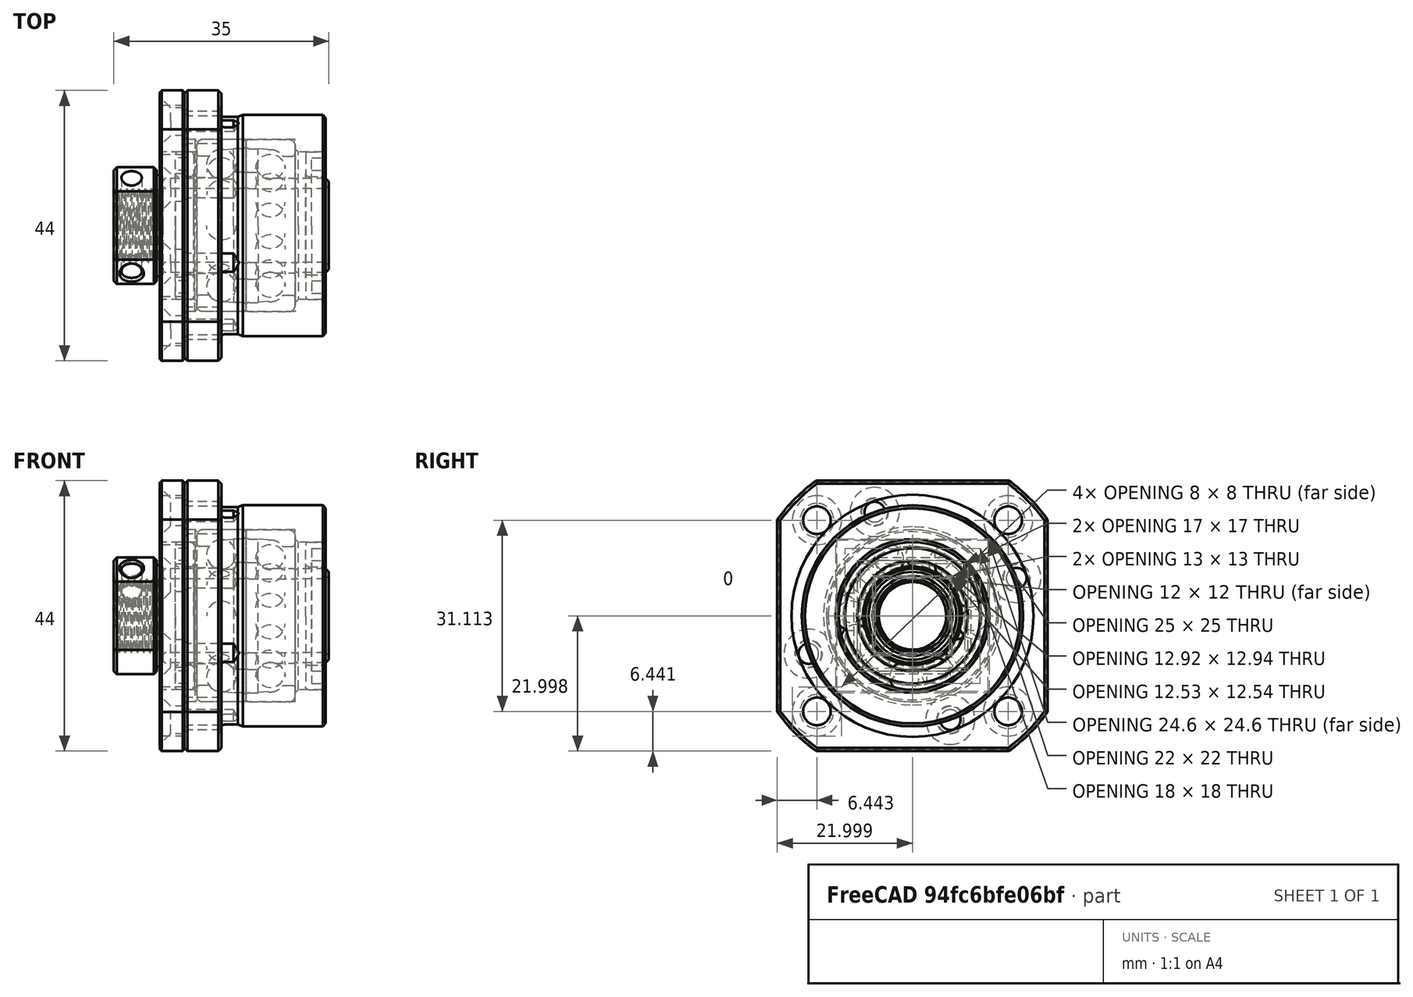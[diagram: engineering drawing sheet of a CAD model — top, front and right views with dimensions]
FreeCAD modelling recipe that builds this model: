
FCSTD DOCUMENT  (FreeCAD 0.21R38887 (Git))
Label: СтанинаСборка
License: All rights reserved
LicenseURL: http://en.wikipedia.org/wiki/All_rights_reserved
objects: Part::FeaturePython×151, App::FeaturePython×121, Part::Feature×35, App::LinkElement×20, App::Link×12, Part::Compound2×1
note: 182 computed .brp shape members not serialized (recipe doc carries the construction recipe); baked Part::Feature solids carry a one-line shape summary decoded from their .brp
EXTERNAL_REF file=ПластинаY.FCStd obj=Body
EXTERNAL_REF file=ПластинаY2.FCStd obj=Body
EXTERNAL_REF file=NEMA23.FCStd obj=Assembly
EXTERNAL_REF file=ТаблицаПараметров.FCStd obj=Spreadsheet001
EXTERNAL_REF file=ТаблицаПараметров.FCStd obj=Spreadsheet007
EXTERNAL_REF file=ЗащитаЛеваяY.FCStd obj=Body
EXTERNAL_REF file=ЗащитаПраваяY.FCStd obj=Body
EXTERNAL_REF file=РоликY.FCStd obj=Assembly
EXTERNAL_REF file=ТаблицаПараметров.FCStd obj=Spreadsheet002
EXTERNAL_REF file=ШВПY.FCStd obj=Cut001
EXTERNAL_REF file=mufta8x10.FCStd obj=Assembly
EXTERNAL_REF file=Крепеж.FCStd obj=Assembly005
EXTERNAL_REF file=Крепеж.FCStd obj=Assembly
EXTERNAL_REF file=Крепеж.FCStd obj=Assembly006

FEATURE [App::Link] Link001  label="PlateY1"
  AutoLinkLabel = true
  AutoPlacement = true
  LinkPlacement = pos=(-19.134,-17.037,0) rot=(0,0,1;0rad)
  LinkedObject = -> <external ПластинаY.FCStd>#Body
  Placement = pos=(-19.134,-17.037,0) rot=(0,0,1;0rad)
  SyncGroupVisibility = false
  TreeRank = 1
  _LinkVersion = 1
FEATURE [App::Link] Link002  label="PlateY2"
  AutoLinkLabel = true
  AutoPlacement = true
  LinkPlacement = pos=(-481.358,-61.5083,250) rot=(0,0,1;0rad)
  LinkedObject = -> <external ПластинаY2.FCStd>#Body
  Placement = pos=(-481.358,-61.5083,250) rot=(0,0,1;0rad)
  SyncGroupVisibility = false
  TreeRank = 2
  _LinkVersion = 1
FEATURE [Part::Feature] Solid
  InvalidShape = false
  TreeRank = 98
  ValidateShape = false
  shape: bbox 9.525 x 13.65 x 18.88 mm, 2 faces (baked)
FEATURE [Part::Feature] Solid001
  InvalidShape = false
  TreeRank = 99
  ValidateShape = false
  shape: bbox 8 x 34.8 x 17.4 mm, 22 faces (baked)
FEATURE [Part::Feature] Solid002
  InvalidShape = false
  TreeRank = 100
  ValidateShape = false
  shape: bbox 9.525 x 19.51 x 7.225 mm, 2 faces (baked)
FEATURE [Part::Feature] Solid003
  InvalidShape = false
  TreeRank = 101
  ValidateShape = false
  shape: bbox 9.525 x 13.65 x 18.88 mm, 2 faces (baked)
FEATURE [Part::Feature] Solid004
  InvalidShape = false
  TreeRank = 102
  ValidateShape = false
  shape: bbox 5.5 x 30.6 x 15.3 mm, 14 faces (baked)
FEATURE [Part::Feature] Solid005
  InvalidShape = false
  TreeRank = 103
  ValidateShape = false
  shape: bbox 9.525 x 15.39 x 18.01 mm, 2 faces (baked)
FEATURE [Part::Feature] Solid006
  InvalidShape = false
  TreeRank = 104
  ValidateShape = false
  shape: bbox 9.525 x 18.88 x 13.65 mm, 2 faces (baked)
FEATURE [Part::Feature] Solid007
  InvalidShape = false
  TreeRank = 105
  ValidateShape = false
  shape: bbox 9.525 x 19.43 x 11.68 mm, 2 faces (baked)
FEATURE [Part::Feature] Solid008
  InvalidShape = false
  TreeRank = 106
  ValidateShape = false
  shape: bbox 9.525 x 18.88 x 13.65 mm, 2 faces (baked)
FEATURE [Part::Feature] Solid009
  InvalidShape = false
  TreeRank = 107
  ValidateShape = false
  shape: bbox 9.525 x 11.68 x 19.43 mm, 2 faces (baked)
FEATURE [Part::Feature] Solid010
  InvalidShape = false
  TreeRank = 108
  ValidateShape = false
  shape: bbox 9.525 x 13.65 x 18.88 mm, 2 faces (baked)
FEATURE [Part::Feature] Solid011
  InvalidShape = false
  TreeRank = 109
  ValidateShape = false
  shape: bbox 9.525 x 4.763 x 19.05 mm, 2 faces (baked)
FEATURE [Part::Feature] Solid012
  InvalidShape = false
  TreeRank = 110
  ValidateShape = false
  shape: bbox 9.525 x 19.51 x 7.225 mm, 2 faces (baked)
FEATURE [Part::Feature] Solid013
  InvalidShape = false
  TreeRank = 111
  ValidateShape = false
  shape: bbox 9.525 x 15.39 x 18.01 mm, 2 faces (baked)
FEATURE [Part::Feature] Solid014
  InvalidShape = false
  TreeRank = 112
  ValidateShape = false
  shape: bbox 9.525 x 18.01 x 15.39 mm, 2 faces (baked)
FEATURE [Part::Feature] Solid015
  InvalidShape = false
  TreeRank = 113
  ValidateShape = false
  shape: bbox 3 x 24 x 48 mm, 20 faces (baked)
FEATURE [Part::Feature] Solid016
  InvalidShape = false
  TreeRank = 114
  ValidateShape = false
  shape: bbox 8 x 47.26 x 62.45 mm, 26 faces (baked)
FEATURE [Part::Feature] Solid017
  InvalidShape = false
  TreeRank = 115
  ValidateShape = false
  shape: bbox 9.525 x 18.01 x 15.39 mm, 2 faces (baked)
FEATURE [Part::Feature] Solid018
  InvalidShape = false
  TreeRank = 116
  ValidateShape = false
  shape: bbox 9.525 x 19.43 x 11.68 mm, 2 faces (baked)
FEATURE [Part::Feature] Solid019
  InvalidShape = false
  TreeRank = 117
  ValidateShape = false
  shape: bbox 9.525 x 13.65 x 18.88 mm, 2 faces (baked)
FEATURE [Part::Feature] Solid020
  InvalidShape = false
  TreeRank = 118
  ValidateShape = false
  shape: bbox 8 x 29.37 x 38.81 mm, 22 faces (baked)
FEATURE [Part::Feature] Solid021
  InvalidShape = false
  TreeRank = 119
  ValidateShape = false
  shape: bbox 8 x 56 x 28 mm, 26 faces (baked)
FEATURE [Part::Feature] Solid022
  InvalidShape = false
  TreeRank = 120
  ValidateShape = false
  shape: bbox 9.525 x 4.763 x 19.05 mm, 2 faces (baked)
FEATURE [Part::Feature] Solid023
  InvalidShape = false
  TreeRank = 121
  ValidateShape = false
  shape: bbox 9.525 x 19.05 x 4.763 mm, 2 faces (baked)
FEATURE [Part::Feature] Solid024
  InvalidShape = false
  TreeRank = 122
  ValidateShape = false
  shape: bbox 3 x 24 x 48 mm, 20 faces (baked)
FEATURE [Part::Feature] Solid025
  InvalidShape = false
  TreeRank = 123
  ValidateShape = false
  shape: bbox 9.525 x 18.88 x 13.65 mm, 2 faces (baked)
FEATURE [Part::Feature] Solid026
  InvalidShape = false
  TreeRank = 124
  ValidateShape = false
  shape: bbox 9.525 x 7.225 x 19.51 mm, 2 faces (baked)
FEATURE [Part::Feature] Solid027
  InvalidShape = false
  TreeRank = 125
  ValidateShape = false
  shape: bbox 9.167 x 19 x 19 mm, 80 faces (baked)
FEATURE [Part::Feature] Solid028
  InvalidShape = false
  TreeRank = 126
  ValidateShape = false
  shape: bbox 9.525 x 11.68 x 19.43 mm, 2 faces (baked)
FEATURE [Part::Feature] Solid029
  InvalidShape = false
  TreeRank = 127
  ValidateShape = false
  shape: bbox 5.5 x 30.6 x 15.3 mm, 14 faces (baked)
FEATURE [Part::Feature] Solid030
  InvalidShape = false
  TreeRank = 128
  ValidateShape = false
  shape: bbox 23 x 44 x 44 mm, 94 faces (baked)
FEATURE [Part::Feature] Solid031
  InvalidShape = false
  TreeRank = 129
  ValidateShape = false
  shape: bbox 9.525 x 18.88 x 13.65 mm, 2 faces (baked)
FEATURE [Part::Feature] Solid032
  InvalidShape = false
  TreeRank = 130
  ValidateShape = false
  shape: bbox 6 x 44 x 44 mm, 61 faces (baked)
FEATURE [Part::Feature] Solid033
  InvalidShape = false
  TreeRank = 131
  ValidateShape = false
  shape: bbox 9.525 x 19.05 x 4.763 mm, 2 faces (baked)
FEATURE [Part::Feature] Solid034
  InvalidShape = false
  TreeRank = 132
  ValidateShape = false
  shape: bbox 9.525 x 7.225 x 19.51 mm, 2 faces (baked)
FEATURE [Part::Compound2] Compound  label="FK12"
  InvalidShape = false
  Links = -> [Solid,Solid001,Solid002,Solid003,Solid004,Solid005,Solid006,Solid007,Solid008,Solid009,Solid010,Solid011,Solid012,Solid013,Solid014,Solid015,Solid016,Solid017,Solid018,Solid019,Solid020,Solid021,Solid022,Solid023,Solid024,Solid025,Solid026,Solid027,Solid028,Solid029,Solid030,Solid031,Solid032,Solid033,Solid034]
  Placement = pos=(282.718,411.762,278.225) rot=(-0.707107,0,-0.707107;3.14159rad)
  TreeRank = 133
  ValidateShape = false
FEATURE [App::Link] Link003  label="NEMA23"
  AutoLinkLabel = true
  AutoPlacement = true
  LinkPlacement = pos=(205.55,418.707,297.9) rot=(0,1,0;3.14159rad)
  LinkedObject = -> <external NEMA23.FCStd>#Assembly
  Placement = pos=(205.55,418.707,297.9) rot=(0,1,0;3.14159rad)
  SyncGroupVisibility = false
  TreeRank = 164
  _LinkVersion = 1
FEATURE [App::Link] Link012  label="ЗащитаСлеваY"
  AutoLinkLabel = false
  AutoPlacement = true
  LinkedObject = -> <external ЗащитаЛеваяY.FCStd>#Body
  SyncGroupVisibility = false
  TreeRank = 458
  _LinkOwner = 1626
  _LinkVersion = 1
FEATURE [App::Link] Link013  label="ЗащитаСправаY"
  AutoLinkLabel = false
  AutoPlacement = true
  LinkPlacement = pos=(1.421e-13,-1.35e-13,223.3) rot=(0,0,1;0rad)
  LinkedObject = -> <external ЗащитаПраваяY.FCStd>#Body
  Placement = pos=(1.421e-13,-1.35e-13,223.3) rot=(0,0,1;0rad)
  SyncGroupVisibility = false
  TreeRank = 459
  _LinkOwner = 1626
  _LinkVersion = 1
FEATURE [App::Link] Link018  label="ШВПY"
  AutoLinkLabel = true
  AutoPlacement = true
  LinkPlacement = pos=(377.35,390.502,185) rot=(1,0,0;1.5708rad)
  LinkedObject = -> <external ШВПY.FCStd>#Cut001
  Placement = pos=(377.35,390.502,185) rot=(1,0,0;1.5708rad)
  SyncGroupVisibility = false
  TreeRank = 610
  _LinkVersion = 1
FEATURE [App::Link] Link019  label="Муфта_8_10мм001"
  AutoLinkLabel = true
  AutoPlacement = true
  LinkPlacement = pos=(390.615,406.393,319.227) rot=(0.199343,-0.787324,-0.583424;3.79561rad)
  LinkedObject = -> <external mufta8x10.FCStd>#Assembly
  Placement = pos=(390.615,406.393,319.227) rot=(0.199343,-0.787324,-0.583424;3.79561rad)
  SyncGroupVisibility = false
  TreeRank = 617
  _LinkVersion = 1
FEATURE [App::LinkElement] Link014_i0
  LinkPlacement = pos=(33.3,-2.65,-2.65) rot=(1,0,0;3.14159rad)
  LinkedObject = -> <external РоликY.FCStd>#Assembly
  Placement = pos=(33.3,-2.65,-2.65) rot=(1,0,0;3.14159rad)
  TreeRank = 818
  _LinkOwner = 1707
  _LinkVersion = 1
FEATURE [App::LinkElement] Link014_i1
  LinkPlacement = pos=(35.1,110.35,-2.65) rot=(0,-1,0;3.14159rad)
  LinkedObject = -> <external РоликY.FCStd>#Assembly
  Placement = pos=(35.1,110.35,-2.65) rot=(0,-1,0;3.14159rad)
  TreeRank = 819
  _LinkOwner = 1707
  _LinkVersion = 1
FEATURE [App::LinkElement] Link014_i2
  LinkPlacement = pos=(33.3,-2.65,511.35) rot=(1,0,0;3.14159rad)
  LinkedObject = -> <external РоликY.FCStd>#Assembly
  Placement = pos=(33.3,-2.65,511.35) rot=(1,0,0;3.14159rad)
  TreeRank = 820
  _LinkOwner = 1707
  _LinkVersion = 1
FEATURE [App::LinkElement] Link014_i3
  LinkPlacement = pos=(33.3,110.35,511.35) rot=(1,0,0;3.14159rad)
  LinkedObject = -> <external РоликY.FCStd>#Assembly
  Placement = pos=(33.3,110.35,511.35) rot=(1,0,0;3.14159rad)
  TreeRank = 821
  _LinkOwner = 1707
  _LinkVersion = 1
FEATURE [App::Link] Link014  label="Ролики"
  AutoLinkLabel = true
  AutoPlacement = true
  ElementCount = 4
  ElementList = -> [Link014_i0,Link014_i1,Link014_i2,Link014_i3]
  LinkPlacement = pos=(-234.35,38.35,78.7) rot=(-0.707107,0,-0.707107;3.14159rad)
  LinkedObject = -> <external РоликY.FCStd>#Assembly
  Placement = pos=(-234.35,38.35,78.7) rot=(-0.707107,0,-0.707107;3.14159rad)
  SyncGroupVisibility = false
  TreeRank = 485
  _LinkVersion = 1
FEATURE [Part::FeaturePython] Parts004  # WARN: FeaturePython — macro-defined, semantics opaque (R4)
  Group = -> [Link012,Link013,Link014]
  GroupMode = 0
  InvalidShape = false
  TreeRank = 457
  ValidateShape = false
  _LinkVersion = 1
FEATURE [App::LinkElement] Link030_i0
  LinkPlacement = pos=(417.35,350.007,2.01454e-09) rot=(0,0,1;0rad)
  LinkedObject = -> <external Крепеж.FCStd>#Assembly005
  Placement = pos=(417.35,350.007,2.01454e-09) rot=(0,0,1;0rad)
  TreeRank = 867
  _LinkOwner = 2156
  _LinkVersion = 1
FEATURE [App::LinkElement] Link030_i1
  LinkPlacement = pos=(417.35,310.007,2.01454e-09) rot=(0,0,1;0rad)
  LinkedObject = -> <external Крепеж.FCStd>#Assembly005
  Placement = pos=(417.35,310.007,2.01454e-09) rot=(0,0,1;0rad)
  TreeRank = 868
  _LinkOwner = 2156
  _LinkVersion = 1
FEATURE [App::LinkElement] Link030_i2
  LinkPlacement = pos=(337.35,310.007,2.01459e-09) rot=(0,0,1;0rad)
  LinkedObject = -> <external Крепеж.FCStd>#Assembly005
  Placement = pos=(337.35,310.007,2.01459e-09) rot=(0,0,1;0rad)
  TreeRank = 869
  _LinkOwner = 2156
  _LinkVersion = 1
FEATURE [App::LinkElement] Link030_i3
  LinkPlacement = pos=(337.35,350.007,2.01458e-09) rot=(0,0,1;0rad)
  LinkedObject = -> <external Крепеж.FCStd>#Assembly005
  Placement = pos=(337.35,350.007,2.01458e-09) rot=(0,0,1;0rad)
  TreeRank = 870
  _LinkOwner = 2156
  _LinkVersion = 1
FEATURE [App::LinkElement] Link030_i4
  LinkPlacement = pos=(337.35,310.007,420) rot=(1,0,0;3.14159rad)
  LinkedObject = -> <external Крепеж.FCStd>#Assembly005
  Placement = pos=(337.35,310.007,420) rot=(1,0,0;3.14159rad)
  TreeRank = 871
  _LinkOwner = 2156
  _LinkVersion = 1
FEATURE [App::LinkElement] Link030_i5
  LinkPlacement = pos=(417.35,310.007,420) rot=(1,0,0;3.14159rad)
  LinkedObject = -> <external Крепеж.FCStd>#Assembly005
  Placement = pos=(417.35,310.007,420) rot=(1,0,0;3.14159rad)
  TreeRank = 872
  _LinkOwner = 2156
  _LinkVersion = 1
FEATURE [App::LinkElement] Link030_i6
  LinkPlacement = pos=(417.35,350.007,420) rot=(1,0,0;3.14159rad)
  LinkedObject = -> <external Крепеж.FCStd>#Assembly005
  Placement = pos=(417.35,350.007,420) rot=(1,0,0;3.14159rad)
  TreeRank = 873
  _LinkOwner = 2156
  _LinkVersion = 1
FEATURE [App::LinkElement] Link030_i7
  LinkPlacement = pos=(337.35,350.007,420) rot=(1,0,0;3.14159rad)
  LinkedObject = -> <external Крепеж.FCStd>#Assembly005
  Placement = pos=(337.35,350.007,420) rot=(1,0,0;3.14159rad)
  TreeRank = 874
  _LinkOwner = 2156
  _LinkVersion = 1
FEATURE [App::Link] Link030  label="КрепежМ6_Тгайка"
  AutoLinkLabel = true
  AutoPlacement = true
  ElementCount = 8
  ElementList = -> [Link030_i0,Link030_i1,Link030_i2,Link030_i3,Link030_i4,Link030_i5,Link030_i6,Link030_i7]
  LinkedObject = -> <external Крепеж.FCStd>#Assembly005
  SyncGroupVisibility = false
  TreeRank = 857
  _LinkVersion = 1
FEATURE [App::LinkElement] Link031_i0
  LinkPlacement = pos=(153.78,414.077,264.8) rot=(0,0,1;3.14159rad)
  LinkedObject = -> <external Крепеж.FCStd>#Assembly
  Placement = pos=(153.78,414.077,264.8) rot=(0,0,1;3.14159rad)
  TreeRank = 909
  _LinkOwner = 2210
  _LinkVersion = 1
FEATURE [App::LinkElement] Link031_i1
  LinkPlacement = pos=(153.78,366.937,264.8) rot=(0,0,1;3.14159rad)
  LinkedObject = -> <external Крепеж.FCStd>#Assembly
  Placement = pos=(153.78,366.937,264.8) rot=(0,0,1;3.14159rad)
  TreeRank = 910
  _LinkOwner = 2210
  _LinkVersion = 1
FEATURE [App::LinkElement] Link031_i2
  LinkPlacement = pos=(200.92,366.937,264.8) rot=(0,0,1;3.14159rad)
  LinkedObject = -> <external Крепеж.FCStd>#Assembly
  Placement = pos=(200.92,366.937,264.8) rot=(0,0,1;3.14159rad)
  TreeRank = 911
  _LinkOwner = 2210
  _LinkVersion = 1
FEATURE [App::LinkElement] Link031_i3
  LinkPlacement = pos=(200.92,414.077,264.8) rot=(0,0,1;3.14159rad)
  LinkedObject = -> <external Крепеж.FCStd>#Assembly
  Placement = pos=(200.92,414.077,264.8) rot=(0,0,1;3.14159rad)
  TreeRank = 912
  _LinkOwner = 2210
  _LinkVersion = 1
FEATURE [App::Link] Link031  label="М5х12"
  AutoLinkLabel = false
  AutoPlacement = true
  ElementCount = 4
  ElementList = -> [Link031_i0,Link031_i1,Link031_i2,Link031_i3]
  LinkedObject = -> <external Крепеж.FCStd>#Assembly
  SyncGroupVisibility = false
  TreeRank = 908
  _LinkVersion = 1
FEATURE [Part::FeaturePython] Parts002  # WARN: FeaturePython — macro-defined, semantics opaque (R4)
  Group = -> [Link003,Link002,Link031]
  GroupMode = 0
  InvalidShape = false
  TreeRank = 221
  ValidateShape = false
  _LinkVersion = 1
FEATURE [App::LinkElement] Link032_i0
  LinkPlacement = pos=(194.43,377.469,-6) rot=(-1,0,0;3.14159rad)
  LinkedObject = -> <external Крепеж.FCStd>#Assembly006
  Placement = pos=(194.43,377.469,-6) rot=(-1,0,0;3.14159rad)
  TreeRank = 918
  _LinkOwner = 2219
  _LinkVersion = 1
FEATURE [App::LinkElement] Link032_i1
  LinkPlacement = pos=(194.43,346.356,-6) rot=(-1,0,0;3.14159rad)
  LinkedObject = -> <external Крепеж.FCStd>#Assembly006
  Placement = pos=(194.43,346.356,-6) rot=(-1,0,0;3.14159rad)
  TreeRank = 919
  _LinkOwner = 2219
  _LinkVersion = 1
FEATURE [App::LinkElement] Link032_i2
  LinkPlacement = pos=(225.543,346.356,-6) rot=(-1,0,0;3.14159rad)
  LinkedObject = -> <external Крепеж.FCStd>#Assembly006
  Placement = pos=(225.543,346.356,-6) rot=(-1,0,0;3.14159rad)
  TreeRank = 920
  _LinkOwner = 2219
  _LinkVersion = 1
FEATURE [App::LinkElement] Link032_i3
  LinkPlacement = pos=(225.543,377.469,-6) rot=(-1,0,0;3.14159rad)
  LinkedObject = -> <external Крепеж.FCStd>#Assembly006
  Placement = pos=(225.543,377.469,-6) rot=(-1,0,0;3.14159rad)
  TreeRank = 921
  _LinkOwner = 2219
  _LinkVersion = 1
FEATURE [App::Link] Link032  label="М4х16"
  AutoLinkLabel = true
  AutoPlacement = true
  ElementCount = 4
  ElementList = -> [Link032_i0,Link032_i1,Link032_i2,Link032_i3]
  LinkedObject = -> <external Крепеж.FCStd>#Assembly006
  SyncGroupVisibility = false
  TreeRank = 917
  _LinkVersion = 1
FEATURE [Part::FeaturePython] Parts001  # WARN: FeaturePython — macro-defined, semantics opaque (R4)
  Group = -> [Link001,Compound,Link032]
  GroupMode = 0
  InvalidShape = false
  TreeRank = 217
  ValidateShape = false
  _LinkVersion = 1
FEATURE [App::Link] Link  label="МасивПрофиля"
  AutoLinkLabel = false
  AutoPlacement = true
  LinkPlacement = pos=(0,0,0) rot=(0,1,0;1.5708rad)
  Placement = pos=(0,0,0) rot=(0,1,0;1.5708rad)
  SyncGroupVisibility = false
  TreeRank = 933
  _LinkOwner = 1573
  _LinkVersion = 1
FEATURE [Part::FeaturePython] Assembly001  label="PlateForFK12"  # WARN: FeaturePython — macro-defined, semantics opaque (R4)
  AutoRelax = true
  BuildShape = 0
  Freeze = false
  Group = -> [Constraints001,Elements001,Parts001]
  InvalidShape = false
  Placement = pos=(167.364,28.5944,2.01459e-09) rot=(0,0,1;0rad)
  TreeRank = 214
  ValidateShape = false
  Verbose = false
  _LinkVersion = 1
  _SolverType = 1
  _Version = 1
FEATURE [App::FeaturePython] Constraints001  # WARN: FeaturePython — macro-defined, semantics opaque (R4)
  Group = -> [Constraint004,Constraint001,Constraint018,Constraint021,Constraint020,Constraint019]
  TreeRank = 215
  _LinkVersion = 1
  _Version = 1
FEATURE [App::FeaturePython] Elements001  # WARN: FeaturePython — macro-defined, semantics opaque (R4)
  Group = -> [Element,Element001,Element002,Element003,Element004,Element005,Element006,Element007,Element008,Element009,Element010,_Element,Element032,Element033,Element035,Element036,_Element002,_Element003,_Element004,_Element005,_Element006,_Element007,Element038,Element040,Element041,Element042,Element046,Element082,Element098,Element100,Element102,Element104,_Element060,_Element061,_Element062,+1 more]
  TreeRank = 216
  _LinkVersion = 1
FEATURE [Part::FeaturePython] Assembly002  label="PlateForMotor"  # WARN: FeaturePython — macro-defined, semantics opaque (R4)
  AutoRelax = true
  BuildShape = 0
  Freeze = false
  Group = -> [Constraints002,Elements002,Parts002]
  InvalidShape = false
  Placement = pos=(200,5.45395e-11,160) rot=(0,0,1;0rad)
  TreeRank = 218
  ValidateShape = false
  Verbose = false
  _LinkVersion = 1
  _SolverType = 1
  _Version = 1
FEATURE [App::FeaturePython] Constraints002  # WARN: FeaturePython — macro-defined, semantics opaque (R4)
  Group = -> [Constraint007,Constraint006,Constraint060,Constraint061,Constraint062,Constraint063]
  TreeRank = 219
  _LinkVersion = 1
  _Version = 1
FEATURE [App::FeaturePython] Elements002  # WARN: FeaturePython — macro-defined, semantics opaque (R4)
  Group = -> [Element011,Element012,Element013,Element014,Element015,Element016,Element017,Element018,_Element001,Element021,Element020,Element022,Element023,_Element008,_Element009,Element037,Element039,Element048,Element051,Element073,Element087,Element106,Element108,Element110,Element112,_Element056,_Element057,_Element058,_Element059]
  TreeRank = 220
  _LinkVersion = 1
FEATURE [Part::FeaturePython] Element  # link proxy (typed FeaturePython)
  Detach = false
  InvalidShape = false
  LinkTransform = true
  LinkedObject = -> Compound [Face353]
  TreeRank = 222
  ValidateShape = false
  _LinkVersion = 1
  _Parent = -> Elements001
FEATURE [Part::FeaturePython] Element001  # link proxy (typed FeaturePython)
  Detach = false
  InvalidShape = false
  LinkTransform = true
  LinkedObject = -> Link001 [Pad.Face18]
  TreeRank = 223
  ValidateShape = false
  _LinkVersion = 1
  _Parent = -> Elements001
FEATURE [Part::FeaturePython] Element002  # link proxy (typed FeaturePython)
  Detach = false
  InvalidShape = false
  LinkTransform = true
  LinkedObject = -> Compound [Face313]
  TreeRank = 224
  ValidateShape = false
  _LinkVersion = 1
  _Parent = -> Elements001
FEATURE [Part::FeaturePython] Element003  # link proxy (typed FeaturePython)
  Detach = false
  InvalidShape = false
  LinkTransform = true
  LinkedObject = -> Compound [Face378]
  TreeRank = 225
  ValidateShape = false
  _LinkVersion = 1
  _Parent = -> Elements001
FEATURE [Part::FeaturePython] Element004  # link proxy (typed FeaturePython)
  Detach = false
  InvalidShape = false
  LinkTransform = true
  LinkedObject = -> Compound [Face301]
  TreeRank = 226
  ValidateShape = false
  _LinkVersion = 1
  _Parent = -> Elements001
FEATURE [Part::FeaturePython] Element005  # link proxy (typed FeaturePython)
  Detach = false
  InvalidShape = false
  LinkTransform = true
  LinkedObject = -> Compound [Face337]
  TreeRank = 227
  ValidateShape = false
  _LinkVersion = 1
  _Parent = -> Elements001
FEATURE [Part::FeaturePython] Element006  # link proxy (typed FeaturePython)
  Detach = false
  InvalidShape = false
  LinkTransform = true
  LinkedObject = -> Compound [Face299]
  TreeRank = 228
  ValidateShape = false
  _LinkVersion = 1
  _Parent = -> Elements001
FEATURE [Part::FeaturePython] Element007  # link proxy (typed FeaturePython)
  Detach = false
  InvalidShape = false
  LinkTransform = true
  LinkedObject = -> Compound [Face335]
  TreeRank = 229
  ValidateShape = false
  _LinkVersion = 1
  _Parent = -> Elements001
FEATURE [Part::FeaturePython] Element008  # link proxy (typed FeaturePython)
  Detach = false
  InvalidShape = false
  LinkTransform = true
  LinkedObject = -> Link001 [Pad.Face14]
  TreeRank = 230
  ValidateShape = false
  _LinkVersion = 1
  _Parent = -> Elements001
FEATURE [Part::FeaturePython] Element009  # link proxy (typed FeaturePython)
  Detach = false
  InvalidShape = false
  LinkTransform = true
  LinkedObject = -> Link001 [Pad.Face16]
  TreeRank = 231
  ValidateShape = false
  _LinkVersion = 1
  _Parent = -> Elements001
FEATURE [Part::FeaturePython] Element010  # link proxy (typed FeaturePython)
  Detach = false
  InvalidShape = false
  LinkTransform = true
  LinkedObject = -> Link001 [Pad.Face9]
  TreeRank = 232
  ValidateShape = false
  _LinkVersion = 1
  _Parent = -> Elements001
FEATURE [App::FeaturePython] Constraint001  label="Attachment"  # WARN: FeaturePython — macro-defined, semantics opaque (R4)
  Cascade = false
  Disabled = false
  Group = -> [ElementLink002,ElementLink004]
  Multiply = false
  TreeRank = 236
  _ConstraintType = 45
  _LinkVersion = 1
  _Parent = -> Constraints001
FEATURE [App::FeaturePython] ElementLink002  label="_Element002"  # link proxy (typed FeaturePython)
  LinkTransform = true
  LinkedObject = -> _Element002
  TreeRank = 237
  _LinkVersion = 1
  _Parent = -> Constraint001
FEATURE [App::FeaturePython] ElementLink004  label="_Element010"  # link proxy (typed FeaturePython)
  LinkTransform = true
  LinkedObject = -> _Element003
  TreeRank = 239
  _LinkVersion = 1
  _Parent = -> Constraint001
FEATURE [Part::FeaturePython] _Element  # link proxy (typed FeaturePython)
  Detach = false
  InvalidShape = false
  LinkTransform = true
  LinkedObject = -> Link001 [Pad.Edge9]
  TreeRank = 256
  ValidateShape = false
  _LinkVersion = 1
  _Parent = -> Elements001
FEATURE [App::FeaturePython] Constraint004  label="Locked"  # WARN: FeaturePython — macro-defined, semantics opaque (R4)
  Disabled = false
  Group = -> [ElementLink012]
  TreeRank = 260
  _ConstraintType = 0
  _LinkVersion = 1
  _Parent = -> Constraints001
FEATURE [App::FeaturePython] ElementLink012  label="Element001"  # link proxy (typed FeaturePython)
  LinkTransform = true
  LinkedObject = -> Element001
  TreeRank = 261
  _LinkVersion = 1
  _Parent = -> Constraint004
FEATURE [Part::FeaturePython] Element011  # link proxy (typed FeaturePython)
  Detach = false
  InvalidShape = false
  LinkTransform = true
  LinkedObject = -> Link002 [Chamfer001.Face5]
  TreeRank = 270
  ValidateShape = false
  _LinkVersion = 1
  _Parent = -> Elements002
FEATURE [Part::FeaturePython] Element012  # link proxy (typed FeaturePython)
  Detach = false
  InvalidShape = false
  LinkTransform = true
  LinkedObject = -> Link003 [1.$Element001.]
  TreeRank = 271
  ValidateShape = false
  _LinkVersion = 1
  _Parent = -> Elements002
FEATURE [Part::FeaturePython] Element013  # link proxy (typed FeaturePython)
  Detach = false
  InvalidShape = false
  LinkTransform = true
  LinkedObject = -> Link002 [Chamfer001.Face1]
  TreeRank = 272
  ValidateShape = false
  _LinkVersion = 1
  _Parent = -> Elements002
FEATURE [Part::FeaturePython] Element014  # link proxy (typed FeaturePython)
  Detach = false
  InvalidShape = false
  LinkTransform = true
  LinkedObject = -> Link003 [1.$Element003.]
  TreeRank = 273
  ValidateShape = false
  _LinkVersion = 1
  _Parent = -> Elements002
FEATURE [Part::FeaturePython] Element015  # link proxy (typed FeaturePython)
  Detach = false
  InvalidShape = false
  LinkTransform = true
  LinkedObject = -> Link002 [Chamfer001.Face22]
  TreeRank = 274
  ValidateShape = false
  _LinkVersion = 1
  _Parent = -> Elements002
FEATURE [Part::FeaturePython] Element016  # link proxy (typed FeaturePython)
  Detach = false
  InvalidShape = false
  LinkTransform = true
  LinkedObject = -> Link003 [1.$Element006.]
  TreeRank = 275
  ValidateShape = false
  _LinkVersion = 1
  _Parent = -> Elements002
FEATURE [Part::FeaturePython] Element017  # link proxy (typed FeaturePython)
  Detach = false
  InvalidShape = false
  LinkTransform = true
  LinkedObject = -> Link002 [Chamfer001.Face21]
  TreeRank = 276
  ValidateShape = false
  _LinkVersion = 1
  _Parent = -> Elements002
FEATURE [Part::FeaturePython] Element018  # link proxy (typed FeaturePython)
  Detach = false
  InvalidShape = false
  LinkTransform = true
  LinkedObject = -> Link003 [1.$Element007.]
  TreeRank = 277
  ValidateShape = false
  _LinkVersion = 1
  _Parent = -> Elements002
FEATURE [App::FeaturePython] Constraint006  label="Attachment005"  # WARN: FeaturePython — macro-defined, semantics opaque (R4)
  Cascade = false
  Disabled = false
  Group = -> [ElementLink016,ElementLink018]
  Multiply = false
  TreeRank = 281
  _ConstraintType = 45
  _LinkVersion = 1
  _Parent = -> Constraints002
FEATURE [App::FeaturePython] ElementLink016  label="_Element013"  # link proxy (typed FeaturePython)
  LinkTransform = true
  LinkedObject = -> _Element008
  TreeRank = 282
  _LinkVersion = 1
  _Parent = -> Constraint006
FEATURE [App::FeaturePython] Constraint007  label="Locked001"  # WARN: FeaturePython — macro-defined, semantics opaque (R4)
  Disabled = false
  Group = -> [ElementLink017]
  TreeRank = 283
  _ConstraintType = 0
  _LinkVersion = 1
  _Parent = -> Constraints002
FEATURE [App::FeaturePython] ElementLink017  label="_Element001"  # link proxy (typed FeaturePython)
  LinkTransform = true
  LinkedObject = -> _Element001
  TreeRank = 284
  _LinkVersion = 1
  _Parent = -> Constraint007
FEATURE [Part::FeaturePython] _Element001  # link proxy (typed FeaturePython)
  Detach = false
  InvalidShape = false
  LinkTransform = true
  LinkedObject = -> Link002 [Chamfer001.Face4]
  TreeRank = 285
  ValidateShape = false
  _LinkVersion = 1
  _Parent = -> Elements002
FEATURE [App::FeaturePython] ElementLink018  label="_Element014"  # link proxy (typed FeaturePython)
  LinkTransform = true
  LinkedObject = -> _Element009
  TreeRank = 286
  _LinkVersion = 1
  _Parent = -> Constraint006
FEATURE [Part::FeaturePython] Element020  label="2_plate"  # link proxy (typed FeaturePython)
  Detach = false
  InvalidShape = false
  LinkTransform = true
  LinkedObject = -> Link003 [1.$Element008.]
  TreeRank = 294
  ValidateShape = false
  _LinkVersion = 1
  _Parent = -> Elements002
FEATURE [Part::FeaturePython] Element021  label="1_plate"  # link proxy (typed FeaturePython)
  Detach = false
  InvalidShape = false
  LinkTransform = true
  LinkedObject = -> Link003 [1.$Element009.]
  TreeRank = 313
  ValidateShape = false
  _LinkVersion = 1
  _Parent = -> Elements002
FEATURE [Part::FeaturePython] Element022  label="3_plate"  # link proxy (typed FeaturePython)
  Detach = false
  InvalidShape = false
  LinkTransform = true
  LinkedObject = -> Link003 [1.$Element010.]
  TreeRank = 314
  ValidateShape = false
  _LinkVersion = 1
  _Parent = -> Elements002
FEATURE [Part::FeaturePython] Element023  label="4_plate"  # link proxy (typed FeaturePython)
  Detach = false
  InvalidShape = false
  LinkTransform = true
  LinkedObject = -> Link003 [1.$Element011.]
  TreeRank = 315
  ValidateShape = false
  _LinkVersion = 1
  _Parent = -> Elements002
FEATURE [Part::FeaturePython] Element032  label="1hole"  # link proxy (typed FeaturePython)
  Detach = false
  InvalidShape = false
  LinkTransform = true
  LinkedObject = -> Compound [Edge724]
  TreeRank = 352
  ValidateShape = false
  _LinkVersion = 1
  _Parent = -> Elements001
FEATURE [Part::FeaturePython] Element033  label="2hole"  # link proxy (typed FeaturePython)
  Detach = false
  InvalidShape = false
  LinkTransform = true
  LinkedObject = -> Compound [Edge736]
  TreeRank = 353
  ValidateShape = false
  _LinkVersion = 1
  _Parent = -> Elements001
FEATURE [Part::FeaturePython] Element035  label="3hole"  # link proxy (typed FeaturePython)
  Detach = false
  InvalidShape = false
  LinkTransform = true
  LinkedObject = -> Compound [Edge732]
  TreeRank = 355
  ValidateShape = false
  _LinkVersion = 1
  _Parent = -> Elements001
FEATURE [Part::FeaturePython] Element036  label="4hole"  # link proxy (typed FeaturePython)
  Detach = false
  InvalidShape = false
  LinkTransform = true
  LinkedObject = -> Compound [Edge728]
  TreeRank = 356
  ValidateShape = false
  _LinkVersion = 1
  _Parent = -> Elements001
FEATURE [App::FeaturePython] Constraint018  label="Attachment001"  # WARN: FeaturePython — macro-defined, semantics opaque (R4)
  Cascade = false
  Disabled = false
  Group = -> [ElementLink039,ElementLink040]
  Multiply = false
  TreeRank = 357
  _ConstraintType = 45
  _LinkVersion = 1
  _Parent = -> Constraints001
FEATURE [App::FeaturePython] ElementLink039  label="М4_16_посадка@М4х16@#3"  # link proxy (typed FeaturePython)
  LinkTransform = true
  LinkedObject = -> _Element063
  TreeRank = 358
  _LinkVersion = 1
  _Parent = -> Constraint018
FEATURE [App::FeaturePython] ElementLink040  label="4hole"  # link proxy (typed FeaturePython)
  LinkTransform = true
  LinkedObject = -> Element036
  TreeRank = 359
  _LinkVersion = 1
  _Parent = -> Constraint018
FEATURE [App::FeaturePython] Constraint019  label="Attachment004"  # WARN: FeaturePython — macro-defined, semantics opaque (R4)
  Cascade = false
  Disabled = false
  Group = -> [ElementLink041,ElementLink042]
  Multiply = false
  TreeRank = 360
  _ConstraintType = 45
  _LinkVersion = 1
  _Parent = -> Constraints001
FEATURE [App::FeaturePython] ElementLink041  label="3hole"  # link proxy (typed FeaturePython)
  LinkTransform = true
  LinkedObject = -> Element035
  TreeRank = 361
  _LinkVersion = 1
  _Parent = -> Constraint019
FEATURE [App::FeaturePython] ElementLink042  label="М4_16_посадка@М4х16@#2"  # link proxy (typed FeaturePython)
  LinkTransform = true
  LinkedObject = -> _Element062
  TreeRank = 362
  _LinkVersion = 1
  _Parent = -> Constraint019
FEATURE [App::FeaturePython] Constraint020  label="Attachment003"  # WARN: FeaturePython — macro-defined, semantics opaque (R4)
  Cascade = false
  Disabled = false
  Group = -> [ElementLink043,ElementLink044]
  Multiply = false
  TreeRank = 363
  _ConstraintType = 45
  _LinkVersion = 1
  _Parent = -> Constraints001
FEATURE [App::FeaturePython] ElementLink043  label="М4_16_посадка@М4х16@#1"  # link proxy (typed FeaturePython)
  LinkTransform = true
  LinkedObject = -> _Element061
  TreeRank = 364
  _LinkVersion = 1
  _Parent = -> Constraint020
FEATURE [App::FeaturePython] ElementLink044  label="2hole"  # link proxy (typed FeaturePython)
  LinkTransform = true
  LinkedObject = -> Element033
  TreeRank = 365
  _LinkVersion = 1
  _Parent = -> Constraint020
FEATURE [App::FeaturePython] Constraint021  label="Attachment002"  # WARN: FeaturePython — macro-defined, semantics opaque (R4)
  Cascade = false
  Disabled = false
  Group = -> [ElementLink045,ElementLink046]
  Multiply = false
  TreeRank = 366
  _ConstraintType = 45
  _LinkVersion = 1
  _Parent = -> Constraints001
FEATURE [App::FeaturePython] ElementLink045  label="М4_16_посадка@М4х16@#0"  # link proxy (typed FeaturePython)
  LinkTransform = true
  LinkedObject = -> _Element060
  TreeRank = 367
  _LinkVersion = 1
  _Parent = -> Constraint021
FEATURE [App::FeaturePython] ElementLink046  label="1hole"  # link proxy (typed FeaturePython)
  LinkTransform = true
  LinkedObject = -> Element032
  TreeRank = 368
  _LinkVersion = 1
  _Parent = -> Constraint021
FEATURE [Part::FeaturePython] _Element002  # link proxy (typed FeaturePython)
  Detach = false
  InvalidShape = false
  LinkTransform = true
  LinkedObject = -> Compound [Edge904]
  TreeRank = 384
  ValidateShape = false
  _LinkVersion = 1
  _Parent = -> Elements001
FEATURE [Part::FeaturePython] _Element003  label="_Element010"  # link proxy (typed FeaturePython)
  Detach = false
  InvalidShape = false
  LinkTransform = true
  LinkedObject = -> Link001 [Pad.Edge26]
  TreeRank = 385
  ValidateShape = false
  _LinkVersion = 1
  _Parent = -> Elements001
FEATURE [Part::FeaturePython] _Element004  label="_Element009"  # link proxy (typed FeaturePython)
  Detach = false
  InvalidShape = false
  LinkTransform = true
  LinkedObject = -> Link001 [Pad.Edge47]
  TreeRank = 386
  ValidateShape = false
  _LinkVersion = 1
  _Parent = -> Elements001
FEATURE [Part::FeaturePython] _Element005  # link proxy (typed FeaturePython)
  Detach = false
  InvalidShape = false
  LinkTransform = true
  LinkedObject = -> Compound [Edge770]
  TreeRank = 387
  ValidateShape = false
  _LinkVersion = 1
  _Parent = -> Elements001
FEATURE [Part::FeaturePython] _Element006  # link proxy (typed FeaturePython)
  Detach = false
  InvalidShape = false
  LinkTransform = true
  LinkedObject = -> Compound [Face344]
  TreeRank = 390
  ValidateShape = false
  _LinkVersion = 1
  _Parent = -> Elements001
FEATURE [Part::FeaturePython] _Element007  # link proxy (typed FeaturePython)
  Detach = false
  InvalidShape = false
  LinkTransform = true
  LinkedObject = -> Link001 [Pad.Face7]
  TreeRank = 392
  ValidateShape = false
  _LinkVersion = 1
  _Parent = -> Elements001
FEATURE [Part::FeaturePython] _Element008  label="_Element013"  # link proxy (typed FeaturePython)
  Detach = false
  InvalidShape = false
  LinkTransform = true
  LinkedObject = -> Link002 [Chamfer001.Edge7]
  TreeRank = 393
  ValidateShape = false
  _LinkVersion = 1
  _Parent = -> Elements002
FEATURE [Part::FeaturePython] _Element009  label="_Element014"  # link proxy (typed FeaturePython)
  Detach = false
  InvalidShape = false
  LinkTransform = true
  LinkedObject = -> Link003 [1.$Element002.]
  TreeRank = 394
  ValidateShape = false
  _LinkVersion = 1
  _Parent = -> Elements002
FEATURE [Part::FeaturePython] Element037  # link proxy (typed FeaturePython)
  Detach = false
  InvalidShape = false
  LinkTransform = true
  LinkedObject = -> Link002 [Chamfer001.Edge5]
  TreeRank = 395
  ValidateShape = false
  _LinkVersion = 1
  _Parent = -> Elements002
FEATURE [Part::FeaturePython] Element038  # link proxy (typed FeaturePython)
  Detach = false
  InvalidShape = false
  LinkTransform = true
  LinkedObject = -> Link001 [Pad.Edge27]
  TreeRank = 396
  ValidateShape = false
  _LinkVersion = 1
  _Parent = -> Elements001
FEATURE [Part::FeaturePython] Element039  # link proxy (typed FeaturePython)
  Detach = false
  InvalidShape = false
  LinkTransform = true
  LinkedObject = -> Link002 [Chamfer001.Face7]
  TreeRank = 397
  ValidateShape = false
  _LinkVersion = 1
  _Parent = -> Elements002
FEATURE [Part::FeaturePython] Element040  # link proxy (typed FeaturePython)
  Detach = false
  InvalidShape = false
  LinkTransform = true
  LinkedObject = -> Link001 [Pad.Face5]
  TreeRank = 398
  ValidateShape = false
  _LinkVersion = 1
  _Parent = -> Elements001
FEATURE [Part::FeaturePython] Element041  # link proxy (typed FeaturePython)
  Detach = false
  InvalidShape = false
  LinkTransform = true
  LinkedObject = -> Link001 [Pad.Face19]
  TreeRank = 399
  ValidateShape = false
  _LinkVersion = 1
  _Parent = -> Elements001
FEATURE [Part::FeaturePython] Element042  # link proxy (typed FeaturePython)
  Detach = false
  InvalidShape = false
  LinkTransform = true
  LinkedObject = -> Link001 [Pad.Face3]
  TreeRank = 400
  ValidateShape = false
  _LinkVersion = 1
  _Parent = -> Elements001
FEATURE [Part::FeaturePython] Assembly003  label="СборкаСтанины"  # WARN: FeaturePython — macro-defined, semantics opaque (R4)
  AutoRelax = true
  BuildShape = 0
  Freeze = false
  Group = -> [Constraints003,Elements003,Parts003]
  InvalidShape = false
  TreeRank = 401
  ValidateShape = false
  Verbose = false
  _LinkVersion = 1
  _SolverType = 1
  _Version = 1
FEATURE [App::FeaturePython] Constraints003  # WARN: FeaturePython — macro-defined, semantics opaque (R4)
  Group = -> [Constraint,Constraint022,Constraint023,Constraint024,Constraint025,Constraint026,Constraint041,Constraint042,Constraint043,Constraint044,Constraint045,Constraint046,Constraint079,Constraint080,Constraint081,Constraint082,Constraint083,Constraint084,Constraint085,Constraint086]
  TreeRank = 402
  _LinkVersion = 1
  _Version = 1
FEATURE [App::FeaturePython] Elements003  # WARN: FeaturePython — macro-defined, semantics opaque (R4)
  Group = -> [_Element010,_Element011,_Element012,_Element013,_Element014,_Element015,_Element016,_Element017,_Element018,_Element019,_Element020,_Element021,_Element026,_Element027,_Element028,_Element029,_Element030,_Element031,_Element032,_Element033,_Element034,_Element037,Element081,Element083,Element084,Element086,Element088,Element089,_Element038,Element099,Element101,Element103,Element105,Element107,+18 more]
  TreeRank = 403
  _LinkVersion = 1
FEATURE [Part::FeaturePython] Parts003  label="ЧастиСтанины"  # WARN: FeaturePython — macro-defined, semantics opaque (R4)
  Group = -> [Assembly002,Assembly001,Assembly004,Link018,Link019,Link030,Link]
  GroupMode = 0
  InvalidShape = false
  TreeRank = 404
  ValidateShape = false
  _LinkVersion = 1
FEATURE [Part::FeaturePython] _Element010  # link proxy (typed FeaturePython)
  Detach = false
  InvalidShape = false
  LinkTransform = true
  LinkedObject = -> Assembly001 [1.$Element041.]
  TreeRank = 407
  ValidateShape = false
  _LinkVersion = 1
  _Parent = -> Elements003
FEATURE [Part::FeaturePython] _Element011  # WARN: FeaturePython — macro-defined, semantics opaque (R4)
  Detach = false
  InvalidShape = false
  LinkTransform = true
  TreeRank = 410
  ValidateShape = false
  _LinkVersion = 1
  _Parent = -> Elements003
FEATURE [Part::FeaturePython] _Element012  # link proxy (typed FeaturePython)
  Detach = false
  InvalidShape = false
  LinkTransform = true
  LinkedObject = -> Assembly001 [1.$Element042.]
  TreeRank = 413
  ValidateShape = false
  _LinkVersion = 1
  _Parent = -> Elements003
FEATURE [Part::FeaturePython] _Element013  # WARN: FeaturePython — macro-defined, semantics opaque (R4)
  Detach = false
  InvalidShape = false
  LinkTransform = true
  TreeRank = 416
  ValidateShape = false
  _LinkVersion = 1
  _Parent = -> Elements003
FEATURE [App::FeaturePython] Constraint  label="PlaneAlignment"  # WARN: FeaturePython — macro-defined, semantics opaque (R4)
  Angle = 0
  AnglePitch = 0
  AngleRoll = 0
  Cascade = false
  Disabled = false
  Group = -> [ElementLink,ElementLink047]
  LockAngle = false
  TreeRank = 417
  _ConstraintType = 37
  _LinkVersion = 1
  _Parent = -> Constraints003
FEATURE [App::FeaturePython] ElementLink  label="_Element011"  # link proxy (typed FeaturePython)
  LinkTransform = true
  LinkedObject = -> _Element011
  TreeRank = 418
  _LinkVersion = 1
  _Parent = -> Constraint
FEATURE [App::FeaturePython] ElementLink047  label="_Element010"  # link proxy (typed FeaturePython)
  LinkTransform = true
  LinkedObject = -> _Element010
  TreeRank = 419
  _LinkVersion = 1
  _Parent = -> Constraint
FEATURE [App::FeaturePython] Constraint022  label="PlaneAlignment001"  # WARN: FeaturePython — macro-defined, semantics opaque (R4)
  Angle = 0
  AnglePitch = 0
  AngleRoll = 0
  Cascade = false
  Disabled = false
  Group = -> [ElementLink048,ElementLink049]
  LockAngle = false
  TreeRank = 420
  _ConstraintType = 37
  _LinkVersion = 1
  _Parent = -> Constraints003
FEATURE [App::FeaturePython] ElementLink048  label="_Element012"  # link proxy (typed FeaturePython)
  LinkTransform = true
  LinkedObject = -> _Element012
  TreeRank = 421
  _LinkVersion = 1
  _Parent = -> Constraint022
FEATURE [App::FeaturePython] ElementLink049  label="_Element013"  # link proxy (typed FeaturePython)
  LinkTransform = true
  LinkedObject = -> _Element013
  TreeRank = 422
  _LinkVersion = 1
  _Parent = -> Constraint022
FEATURE [Part::FeaturePython] _Element014  # WARN: FeaturePython — macro-defined, semantics opaque (R4)
  Detach = false
  InvalidShape = false
  LinkTransform = true
  TreeRank = 425
  ValidateShape = false
  _LinkVersion = 1
  _Parent = -> Elements003
FEATURE [Part::FeaturePython] Element046  # link proxy (typed FeaturePython)
  Detach = false
  InvalidShape = false
  LinkTransform = true
  LinkedObject = -> Link001 [Pad.Face1]
  TreeRank = 427
  ValidateShape = false
  _LinkVersion = 1
  _Parent = -> Elements001
FEATURE [Part::FeaturePython] _Element015  # link proxy (typed FeaturePython)
  Detach = false
  InvalidShape = false
  LinkTransform = true
  LinkedObject = -> Assembly001 [1.$Element046.]
  TreeRank = 428
  ValidateShape = false
  _LinkVersion = 1
  _Parent = -> Elements003
FEATURE [App::FeaturePython] Constraint023  label="PlaneAlignment002"  # WARN: FeaturePython — macro-defined, semantics opaque (R4)
  Angle = 0
  AnglePitch = 0
  AngleRoll = 0
  Cascade = false
  Disabled = false
  Group = -> [ElementLink050,ElementLink051]
  LockAngle = false
  Offset = -170
  TreeRank = 429
  _ConstraintType = 37
  _LinkVersion = 1
  _Parent = -> Constraints003
  expr: Offset = -(ТаблицаПараметров#<<ТаблСтанина>>.ShirinaStaninu - <<ТаблицаПараметров>>#<<ПластиныY>>.Len1) / 2
FEATURE [App::FeaturePython] ElementLink050  label="_Element015"  # link proxy (typed FeaturePython)
  LinkTransform = true
  LinkedObject = -> _Element015
  TreeRank = 430
  _LinkVersion = 1
  _Parent = -> Constraint023
FEATURE [App::FeaturePython] ElementLink051  label="_Element014"  # link proxy (typed FeaturePython)
  LinkTransform = true
  LinkedObject = -> _Element014
  TreeRank = 431
  _LinkVersion = 1
  _Parent = -> Constraint023
FEATURE [App::FeaturePython] Constraint024  label="PlaneAlignment003"  # WARN: FeaturePython — macro-defined, semantics opaque (R4)
  Angle = 0
  AnglePitch = 0
  AngleRoll = 0
  Cascade = false
  Disabled = false
  Group = -> [ElementLink052,ElementLink053]
  LockAngle = false
  Offset = -720
  TreeRank = 432
  _ConstraintType = 37
  _LinkVersion = 1
  _Parent = -> Constraints003
  expr: Offset = -(<<ТаблицаПараметров>>#<<ТаблСтанина>>.NumberProfileBody - 1) * 80
FEATURE [App::FeaturePython] ElementLink052  label="_Element016"  # link proxy (typed FeaturePython)
  LinkTransform = true
  LinkedObject = -> _Element016
  TreeRank = 433
  _LinkVersion = 1
  _Parent = -> Constraint024
FEATURE [Part::FeaturePython] _Element016  # WARN: FeaturePython — macro-defined, semantics opaque (R4)
  Detach = false
  InvalidShape = false
  LinkTransform = true
  TreeRank = 435
  ValidateShape = false
  _LinkVersion = 1
  _Parent = -> Elements003
FEATURE [App::FeaturePython] ElementLink053  label="_Element017"  # link proxy (typed FeaturePython)
  LinkTransform = true
  LinkedObject = -> _Element017
  TreeRank = 436
  _LinkVersion = 1
  _Parent = -> Constraint024
FEATURE [Part::FeaturePython] _Element017  # link proxy (typed FeaturePython)
  Detach = false
  InvalidShape = false
  LinkTransform = true
  LinkedObject = -> Assembly002 [1.$_Element001.]
  TreeRank = 437
  ValidateShape = false
  _LinkVersion = 1
  _Parent = -> Elements003
FEATURE [App::FeaturePython] Constraint025  label="PlaneAlignment004"  # WARN: FeaturePython — macro-defined, semantics opaque (R4)
  Angle = 0
  AnglePitch = 0
  AngleRoll = 0
  Cascade = false
  Disabled = false
  Group = -> [ElementLink054,ElementLink055]
  LockAngle = false
  TreeRank = 438
  _ConstraintType = 37
  _LinkVersion = 1
  _Parent = -> Constraints003
FEATURE [App::FeaturePython] ElementLink054  label="_Element018"  # link proxy (typed FeaturePython)
  LinkTransform = true
  LinkedObject = -> _Element018
  TreeRank = 439
  _LinkVersion = 1
  _Parent = -> Constraint025
FEATURE [Part::FeaturePython] Element048  # link proxy (typed FeaturePython)
  Detach = false
  InvalidShape = false
  LinkTransform = true
  LinkedObject = -> Link002 [Chamfer001.Face13]
  TreeRank = 440
  ValidateShape = false
  _LinkVersion = 1
  _Parent = -> Elements002
FEATURE [Part::FeaturePython] _Element018  # link proxy (typed FeaturePython)
  Detach = false
  InvalidShape = false
  LinkTransform = true
  LinkedObject = -> Assembly002 [1.$Element048.]
  TreeRank = 441
  ValidateShape = false
  _LinkVersion = 1
  _Parent = -> Elements003
FEATURE [App::FeaturePython] ElementLink055  label="_Element019"  # link proxy (typed FeaturePython)
  LinkTransform = true
  LinkedObject = -> _Element019
  TreeRank = 442
  _LinkVersion = 1
  _Parent = -> Constraint025
FEATURE [Part::FeaturePython] _Element019  # WARN: FeaturePython — macro-defined, semantics opaque (R4)
  Detach = false
  InvalidShape = false
  LinkTransform = true
  TreeRank = 444
  ValidateShape = false
  _LinkVersion = 1
  _Parent = -> Elements003
FEATURE [App::FeaturePython] Constraint026  label="PlaneAlignment005"  # WARN: FeaturePython — macro-defined, semantics opaque (R4)
  Angle = 0
  AnglePitch = 0
  AngleRoll = 0
  Cascade = false
  Disabled = false
  Group = -> [ElementLink057,ElementLink056]
  LockAngle = false
  Offset = -170
  TreeRank = 445
  _ConstraintType = 37
  _LinkVersion = 1
  _Parent = -> Constraints003
  expr: Offset = -(ТаблицаПараметров#<<ТаблСтанина>>.ShirinaStaninu - <<ТаблицаПараметров>>#<<ПластиныY>>.Len1) / 2
FEATURE [App::FeaturePython] ElementLink056  label="_Element020"  # link proxy (typed FeaturePython)
  LinkTransform = true
  LinkedObject = -> _Element020
  TreeRank = 446
  _LinkVersion = 1
  _Parent = -> Constraint026
FEATURE [Part::FeaturePython] _Element020  # WARN: FeaturePython — macro-defined, semantics opaque (R4)
  Detach = false
  InvalidShape = false
  LinkTransform = true
  TreeRank = 448
  ValidateShape = false
  _LinkVersion = 1
  _Parent = -> Elements003
FEATURE [App::FeaturePython] ElementLink057  label="_Element021"  # link proxy (typed FeaturePython)
  LinkTransform = true
  LinkedObject = -> _Element021
  TreeRank = 449
  _LinkVersion = 1
  _Parent = -> Constraint026
FEATURE [Part::FeaturePython] Element051  # link proxy (typed FeaturePython)
  Detach = false
  InvalidShape = false
  LinkTransform = true
  LinkedObject = -> Link002 [Chamfer001.Face11]
  TreeRank = 450
  ValidateShape = false
  _LinkVersion = 1
  _Parent = -> Elements002
FEATURE [Part::FeaturePython] _Element021  # link proxy (typed FeaturePython)
  Detach = false
  InvalidShape = false
  LinkTransform = true
  LinkedObject = -> Assembly002 [1.$Element051.]
  TreeRank = 451
  ValidateShape = false
  _LinkVersion = 1
  _Parent = -> Elements003
FEATURE [Part::FeaturePython] Assembly004  label="СборкаЗащита"  # WARN: FeaturePython — macro-defined, semantics opaque (R4)
  AutoRelax = true
  BuildShape = 0
  Freeze = false
  Group = -> [Constraints004,Elements004,Parts004]
  InvalidShape = false
  Placement = pos=(489.55,370.007,210) rot=(0,-1,0;1.5708rad)
  TreeRank = 551
  ValidateShape = false
  Verbose = false
  _LinkVersion = 1
  _SolverType = 1
  _Version = 1
FEATURE [App::FeaturePython] Constraints004  # WARN: FeaturePython — macro-defined, semantics opaque (R4)
  Group = -> [Constraint039,Constraint064,Constraint074,Constraint075,Constraint076,Constraint077,Constraint078]
  TreeRank = 455
  _LinkVersion = 1
  _Version = 1
FEATURE [App::FeaturePython] Elements004  # WARN: FeaturePython — macro-defined, semantics opaque (R4)
  Group = -> [Element052,Element053,Element054,Element055,Element056,Element057,Element058,Element059,_Element022,Element068,Element070,Element072,_Element024,_Element025,Element075,Element076,Element078,Element079,Element143,_Element051,_Element052,_Element053,_Element054,_Element055,Element155,Element157]
  TreeRank = 456
  _LinkVersion = 1
FEATURE [Part::FeaturePython] Element052  label="ЛПлЛВ"  # link proxy (typed FeaturePython)
  Detach = false
  InvalidShape = false
  LinkTransform = true
  LinkedObject = -> Link012 [LinearPattern.Edge50]
  TreeRank = 464
  ValidateShape = false
  _LinkVersion = 1
  _Parent = -> Elements004
FEATURE [Part::FeaturePython] Element053  label="ЛПлЛН"  # link proxy (typed FeaturePython)
  Detach = false
  InvalidShape = false
  LinkTransform = true
  LinkedObject = -> Link012 [LinearPattern.Edge44]
  TreeRank = 465
  ValidateShape = false
  _LinkVersion = 1
  _Parent = -> Elements004
FEATURE [Part::FeaturePython] Element054  label="ЛПлПВ"  # link proxy (typed FeaturePython)
  Detach = false
  InvalidShape = false
  LinkTransform = true
  LinkedObject = -> Link012 [LinearPattern.Edge54]
  TreeRank = 466
  ValidateShape = false
  _LinkVersion = 1
  _Parent = -> Elements004
FEATURE [Part::FeaturePython] Element055  label="ЛПлПН"  # link proxy (typed FeaturePython)
  Detach = false
  InvalidShape = false
  LinkTransform = true
  LinkedObject = -> Link012 [LinearPattern.Edge45]
  TreeRank = 467
  ValidateShape = false
  _LinkVersion = 1
  _Parent = -> Elements004
FEATURE [Part::FeaturePython] Element056  label="ППлЛВ"  # link proxy (typed FeaturePython)
  Detach = false
  InvalidShape = false
  LinkTransform = true
  LinkedObject = -> Link013 [LinearPattern.Edge28]
  TreeRank = 468
  ValidateShape = false
  _LinkVersion = 1
  _Parent = -> Elements004
FEATURE [Part::FeaturePython] Element057  label="ППлЛН"  # link proxy (typed FeaturePython)
  Detach = false
  InvalidShape = false
  LinkTransform = true
  LinkedObject = -> Link013 [LinearPattern.Edge22]
  TreeRank = 469
  ValidateShape = false
  _LinkVersion = 1
  _Parent = -> Elements004
FEATURE [Part::FeaturePython] Element058  label="ППлПВ"  # link proxy (typed FeaturePython)
  Detach = false
  InvalidShape = false
  LinkTransform = true
  LinkedObject = -> Link013 [LinearPattern.Edge32]
  TreeRank = 470
  ValidateShape = false
  _LinkVersion = 1
  _Parent = -> Elements004
FEATURE [Part::FeaturePython] Element059  label="ППлПН"  # link proxy (typed FeaturePython)
  Detach = false
  InvalidShape = false
  LinkTransform = true
  LinkedObject = -> Link013 [LinearPattern.Edge23]
  TreeRank = 471
  ValidateShape = false
  _LinkVersion = 1
  _Parent = -> Elements004
FEATURE [Part::FeaturePython] Element068  # link proxy (typed FeaturePython)
  Detach = false
  InvalidShape = false
  LinkTransform = true
  LinkedObject = -> Link012 [LinearPattern.Face1]
  TreeRank = 522
  ValidateShape = false
  _LinkVersion = 1
  _Parent = -> Elements004
FEATURE [Part::FeaturePython] Element070  # link proxy (typed FeaturePython)
  Detach = false
  InvalidShape = false
  LinkTransform = true
  LinkedObject = -> Link013 [LinearPattern.Edge4]
  TreeRank = 524
  ValidateShape = false
  _LinkVersion = 1
  _Parent = -> Elements004
FEATURE [Part::FeaturePython] Element072  # link proxy (typed FeaturePython)
  Detach = false
  InvalidShape = false
  LinkTransform = true
  LinkedObject = -> Link013 [LinearPattern.Face1]
  TreeRank = 526
  ValidateShape = false
  _LinkVersion = 1
  _Parent = -> Elements004
FEATURE [App::FeaturePython] Constraint039  label="SameOrientation"  # WARN: FeaturePython — macro-defined, semantics opaque (R4)
  Disabled = false
  Group = -> [ElementLink083,ElementLink084]
  TreeRank = 538
  _ConstraintType = 2
  _LinkVersion = 1
  _Parent = -> Constraints004
FEATURE [App::FeaturePython] ElementLink083  label="_Element024"  # link proxy (typed FeaturePython)
  LinkTransform = true
  LinkedObject = -> _Element024
  TreeRank = 539
  _LinkVersion = 1
  _Parent = -> Constraint039
FEATURE [Part::FeaturePython] _Element024  # link proxy (typed FeaturePython)
  Detach = false
  InvalidShape = false
  LinkTransform = true
  LinkedObject = -> Link013 [LinearPattern.Face16]
  TreeRank = 540
  ValidateShape = false
  _LinkVersion = 1
  _Parent = -> Elements004
FEATURE [App::FeaturePython] ElementLink084  label="_Element025"  # link proxy (typed FeaturePython)
  LinkTransform = true
  LinkedObject = -> _Element025
  TreeRank = 541
  _LinkVersion = 1
  _Parent = -> Constraint039
FEATURE [Part::FeaturePython] _Element025  # link proxy (typed FeaturePython)
  Detach = false
  InvalidShape = false
  LinkTransform = true
  LinkedObject = -> Link012 [LinearPattern.Face16]
  TreeRank = 542
  ValidateShape = false
  _LinkVersion = 1
  _Parent = -> Elements004
FEATURE [Part::FeaturePython] Element073  # link proxy (typed FeaturePython)
  Detach = false
  InvalidShape = false
  LinkTransform = true
  LinkedObject = -> Link002 [Chamfer001.Edge32]
  TreeRank = 557
  ValidateShape = false
  _LinkVersion = 1
  _Parent = -> Elements002
FEATURE [Part::FeaturePython] _Element026  # link proxy (typed FeaturePython)
  Detach = false
  InvalidShape = false
  LinkTransform = true
  LinkedObject = -> Assembly002 [1.$Element073.]
  TreeRank = 558
  ValidateShape = false
  _LinkVersion = 1
  _Parent = -> Elements003
FEATURE [Part::FeaturePython] _Element027  # WARN: FeaturePython — macro-defined, semantics opaque (R4)
  Detach = false
  InvalidShape = false
  LinkTransform = true
  TreeRank = 562
  ValidateShape = false
  _LinkVersion = 1
  _Parent = -> Elements003
FEATURE [Part::FeaturePython] Element075  # link proxy (typed FeaturePython)
  Detach = false
  InvalidShape = false
  LinkTransform = true
  LinkedObject = -> Link012 [LinearPattern.Face6]
  TreeRank = 564
  ValidateShape = false
  _LinkVersion = 1
  _Parent = -> Elements004
FEATURE [Part::FeaturePython] _Element028  # link proxy (typed FeaturePython)
  Detach = false
  InvalidShape = false
  LinkTransform = true
  LinkedObject = -> Assembly004 [1.$Element075.]
  TreeRank = 565
  ValidateShape = false
  _LinkVersion = 1
  _Parent = -> Elements003
FEATURE [Part::FeaturePython] Element076  # link proxy (typed FeaturePython)
  Detach = false
  InvalidShape = false
  LinkTransform = true
  LinkedObject = -> Link013 [LinearPattern.Face6]
  TreeRank = 567
  ValidateShape = false
  _LinkVersion = 1
  _Parent = -> Elements004
FEATURE [Part::FeaturePython] _Element029  # link proxy (typed FeaturePython)
  Detach = false
  InvalidShape = false
  LinkTransform = true
  LinkedObject = -> Assembly004 [1.$Element076.]
  TreeRank = 568
  ValidateShape = false
  _LinkVersion = 1
  _Parent = -> Elements003
FEATURE [Part::FeaturePython] _Element030  # WARN: FeaturePython — macro-defined, semantics opaque (R4)
  Detach = false
  InvalidShape = false
  LinkTransform = true
  TreeRank = 572
  ValidateShape = false
  _LinkVersion = 1
  _Parent = -> Elements003
FEATURE [Part::FeaturePython] _Element031  # link proxy (typed FeaturePython)
  Detach = false
  InvalidShape = false
  LinkTransform = true
  LinkedObject = -> Assembly004 [1.$Element072.]
  TreeRank = 574
  ValidateShape = false
  _LinkVersion = 1
  _Parent = -> Elements003
FEATURE [Part::FeaturePython] _Element032  # link proxy (typed FeaturePython)
  Detach = false
  InvalidShape = false
  LinkTransform = true
  LinkedObject = -> Assembly004 [1.$Element068.]
  TreeRank = 576
  ValidateShape = false
  _LinkVersion = 1
  _Parent = -> Elements003
FEATURE [App::FeaturePython] Constraint041  label="PlaneAlignment006"  # WARN: FeaturePython — macro-defined, semantics opaque (R4)
  Angle = 0
  AnglePitch = 0
  AngleRoll = 0
  Cascade = false
  Disabled = false
  Group = -> [ElementLink087,ElementLink088]
  LockAngle = false
  TreeRank = 577
  _ConstraintType = 37
  _LinkVersion = 1
  _Parent = -> Constraints003
FEATURE [App::FeaturePython] ElementLink087  label="_Element027"  # link proxy (typed FeaturePython)
  LinkTransform = true
  LinkedObject = -> _Element027
  TreeRank = 578
  _LinkVersion = 1
  _Parent = -> Constraint041
FEATURE [App::FeaturePython] ElementLink088  label="_Element029"  # link proxy (typed FeaturePython)
  LinkTransform = true
  LinkedObject = -> _Element029
  TreeRank = 579
  _LinkVersion = 1
  _Parent = -> Constraint041
FEATURE [Part::FeaturePython] Element078  # link proxy (typed FeaturePython)
  Detach = false
  InvalidShape = false
  LinkTransform = true
  LinkedObject = -> Link012 [LinearPattern.?Face5]
  TreeRank = 587
  ValidateShape = false
  _LinkVersion = 1
  _Parent = -> Elements004
FEATURE [Part::FeaturePython] _Element033  # link proxy (typed FeaturePython)
  Detach = false
  InvalidShape = false
  LinkTransform = true
  LinkedObject = -> Assembly004 [1.$Element078.]
  TreeRank = 588
  ValidateShape = false
  _LinkVersion = 1
  _Parent = -> Elements003
FEATURE [Part::FeaturePython] Element079  # link proxy (typed FeaturePython)
  Detach = false
  InvalidShape = false
  LinkTransform = true
  LinkedObject = -> Link013 [LinearPattern.?Face4]
  TreeRank = 591
  ValidateShape = false
  _LinkVersion = 1
  _Parent = -> Elements004
FEATURE [Part::FeaturePython] _Element034  # link proxy (typed FeaturePython)
  Detach = false
  InvalidShape = false
  LinkTransform = true
  LinkedObject = -> Assembly004 [1.$Element079.]
  TreeRank = 592
  ValidateShape = false
  _LinkVersion = 1
  _Parent = -> Elements003
FEATURE [App::FeaturePython] Constraint042  label="PlaneAlignment007"  # WARN: FeaturePython — macro-defined, semantics opaque (R4)
  Angle = 0
  AnglePitch = 0
  AngleRoll = 0
  Cascade = false
  Disabled = false
  Group = -> [ElementLink090,ElementLink092]
  LockAngle = false
  TreeRank = 599
  _ConstraintType = 37
  _LinkVersion = 1
  _Parent = -> Constraints003
FEATURE [App::FeaturePython] ElementLink090  label="_Element030"  # link proxy (typed FeaturePython)
  LinkTransform = true
  LinkedObject = -> _Element030
  TreeRank = 600
  _LinkVersion = 1
  _Parent = -> Constraint042
FEATURE [Part::FeaturePython] _Element037  # link proxy (typed FeaturePython)
  Detach = false
  InvalidShape = false
  LinkTransform = true
  LinkedObject = -> Assembly004 [1.$_Element022.]
  TreeRank = 603
  ValidateShape = false
  _LinkVersion = 1
  _Parent = -> Elements003
FEATURE [App::FeaturePython] ElementLink092  label="_Element031"  # link proxy (typed FeaturePython)
  LinkTransform = true
  LinkedObject = -> _Element031
  TreeRank = 604
  _LinkVersion = 1
  _Parent = -> Constraint042
FEATURE [App::FeaturePython] Constraint043  label="PlaneAlignment008"  # WARN: FeaturePython — macro-defined, semantics opaque (R4)
  Angle = 0
  AnglePitch = 0
  AngleRoll = 0
  Cascade = false
  Disabled = false
  Group = -> [ElementLink094,ElementLink093]
  LockAngle = false
  Offset = 128.9
  TreeRank = 605
  _ConstraintType = 37
  _LinkVersion = 1
  _Parent = -> Constraints003
  expr: Offset = (ТаблицаПараметров#<<ТаблСтанина>>.ShirinaStaninu - <<ТаблицаПараметров>>#<<Ролик>>.dimL1 - 0.2) / 2
FEATURE [App::FeaturePython] ElementLink093  label="_Element020"  # link proxy (typed FeaturePython)
  LinkTransform = true
  LinkedObject = -> _Element020
  TreeRank = 606
  _LinkVersion = 1
  _Parent = -> Constraint043
FEATURE [App::FeaturePython] ElementLink094  label="_Element034"  # link proxy (typed FeaturePython)
  LinkTransform = true
  LinkedObject = -> _Element034
  TreeRank = 607
  _LinkVersion = 1
  _Parent = -> Constraint043
FEATURE [App::FeaturePython] Constraint044  label="Locked004"  # WARN: FeaturePython — macro-defined, semantics opaque (R4)
  Disabled = false
  Group = -> [ElementLink095]
  TreeRank = 608
  _ConstraintType = 0
  _LinkVersion = 1
  _Parent = -> Constraints003
FEATURE [App::FeaturePython] ElementLink095  label="_Element030"  # link proxy (typed FeaturePython)
  LinkTransform = true
  LinkedObject = -> _Element030
  TreeRank = 609
  _LinkVersion = 1
  _Parent = -> Constraint044
FEATURE [Part::FeaturePython] Element081  # link proxy (typed FeaturePython)
  Detach = false
  InvalidShape = false
  LinkTransform = true
  LinkedObject = -> Link018 [Face34]
  TreeRank = 611
  ValidateShape = false
  _LinkVersion = 1
  _Parent = -> Elements003
FEATURE [Part::FeaturePython] Element082  # link proxy (typed FeaturePython)
  Detach = false
  InvalidShape = false
  LinkTransform = true
  LinkedObject = -> Compound [Face283]
  TreeRank = 612
  ValidateShape = false
  _LinkVersion = 1
  _Parent = -> Elements001
FEATURE [Part::FeaturePython] Element083  # link proxy (typed FeaturePython)
  Detach = false
  InvalidShape = false
  LinkTransform = true
  LinkedObject = -> Assembly001 [1.$Element082.]
  TreeRank = 613
  ValidateShape = false
  _LinkVersion = 1
  _Parent = -> Elements003
FEATURE [App::FeaturePython] Constraint045  label="Attachment015"  # WARN: FeaturePython — macro-defined, semantics opaque (R4)
  Cascade = false
  Disabled = false
  Group = -> [ElementLink096,ElementLink097]
  Multiply = false
  TreeRank = 614
  _ConstraintType = 45
  _LinkVersion = 1
  _Parent = -> Constraints003
FEATURE [App::FeaturePython] ElementLink096  label="Element083"  # link proxy (typed FeaturePython)
  LinkTransform = true
  LinkedObject = -> Element083
  TreeRank = 615
  _LinkVersion = 1
  _Parent = -> Constraint045
FEATURE [App::FeaturePython] ElementLink097  label="Element081"  # link proxy (typed FeaturePython)
  LinkTransform = true
  LinkedObject = -> Element081
  TreeRank = 616
  _LinkVersion = 1
  _Parent = -> Constraint045
FEATURE [Part::FeaturePython] Element084  label="muft8mm"  # link proxy (typed FeaturePython)
  Detach = false
  InvalidShape = false
  LinkTransform = true
  LinkedObject = -> Link019 [1.$Element.]
  TreeRank = 618
  ValidateShape = false
  _LinkVersion = 1
  _Parent = -> Elements003
FEATURE [Part::FeaturePython] Element086  label="швп10мм"  # link proxy (typed FeaturePython)
  Detach = false
  InvalidShape = false
  LinkTransform = true
  LinkedObject = -> Link018 [Edge511]
  TreeRank = 620
  ValidateShape = false
  _LinkVersion = 1
  _Parent = -> Elements003
FEATURE [Part::FeaturePython] Element087  # link proxy (typed FeaturePython)
  Detach = false
  InvalidShape = false
  LinkTransform = true
  LinkedObject = -> Link003 [1.$Element012.]
  TreeRank = 621
  ValidateShape = false
  _LinkVersion = 1
  _Parent = -> Elements002
FEATURE [Part::FeaturePython] Element088  label="мотор8мм"  # link proxy (typed FeaturePython)
  Detach = false
  InvalidShape = false
  LinkTransform = true
  LinkedObject = -> Assembly002 [1.$Element087.]
  TreeRank = 622
  ValidateShape = false
  _LinkVersion = 1
  _Parent = -> Elements003
FEATURE [Part::FeaturePython] Element089  label="муфта10мм"  # link proxy (typed FeaturePython)
  Detach = false
  InvalidShape = false
  LinkTransform = true
  LinkedObject = -> Link019 [1.$Element002.]
  TreeRank = 623
  ValidateShape = false
  _LinkVersion = 1
  _Parent = -> Elements003
FEATURE [App::FeaturePython] Constraint046  label="Attachment016"  # WARN: FeaturePython — macro-defined, semantics opaque (R4)
  Cascade = false
  Disabled = false
  Group = -> [ElementLink100,ElementLink101]
  Multiply = false
  TreeRank = 624
  _ConstraintType = 45
  _LinkVersion = 1
  _Parent = -> Constraints003
FEATURE [App::FeaturePython] ElementLink100  label="_Element038"  # link proxy (typed FeaturePython)
  LinkTransform = true
  LinkedObject = -> _Element038
  TreeRank = 627
  _LinkVersion = 1
  _Parent = -> Constraint046
FEATURE [Part::FeaturePython] _Element038  # link proxy (typed FeaturePython)
  Detach = false
  InvalidShape = false
  LinkTransform = true
  LinkedObject = -> Link018 [Face255]
  TreeRank = 883
  ValidateShape = false
  _LinkVersion = 1
  _Parent = -> Elements003
FEATURE [App::FeaturePython] ElementLink101  label="муфта10мм"  # link proxy (typed FeaturePython)
  LinkTransform = true
  LinkedObject = -> Element089
  Offset = pos=(0,0,0) rot=(1,0,0;3.14159rad)
  Placement = pos=(1.4211e-12,782.272,757) rot=(1,0,0;3.14159rad)
  TreeRank = 629
  _LinkVersion = 1
  _Parent = -> Constraint046
FEATURE [Part::FeaturePython] Element098  # link proxy (typed FeaturePython)
  Detach = false
  InvalidShape = false
  LinkTransform = true
  LinkedObject = -> Link001 [Pad.Edge38]
  TreeRank = 652
  ValidateShape = false
  _LinkVersion = 1
  _Parent = -> Elements001
FEATURE [Part::FeaturePython] Element099  label="HoleM6_1"  # link proxy (typed FeaturePython)
  Detach = false
  InvalidShape = false
  LinkTransform = true
  LinkedObject = -> Assembly001 [1.$Element098.]
  TreeRank = 653
  ValidateShape = false
  _LinkVersion = 1
  _Parent = -> Elements003
FEATURE [Part::FeaturePython] Element100  # link proxy (typed FeaturePython)
  Detach = false
  InvalidShape = false
  LinkTransform = true
  LinkedObject = -> Link001 [Pad.Edge35]
  TreeRank = 657
  ValidateShape = false
  _LinkVersion = 1
  _Parent = -> Elements001
FEATURE [Part::FeaturePython] Element101  label="HoleM6_2"  # link proxy (typed FeaturePython)
  Detach = false
  InvalidShape = false
  LinkTransform = true
  LinkedObject = -> Assembly001 [1.$Element100.]
  TreeRank = 658
  ValidateShape = false
  _LinkVersion = 1
  _Parent = -> Elements003
FEATURE [Part::FeaturePython] Element102  # link proxy (typed FeaturePython)
  Detach = false
  InvalidShape = false
  LinkTransform = true
  LinkedObject = -> Link001 [Pad.Edge32]
  TreeRank = 659
  ValidateShape = false
  _LinkVersion = 1
  _Parent = -> Elements001
FEATURE [Part::FeaturePython] Element103  label="HoleM6_3"  # link proxy (typed FeaturePython)
  Detach = false
  InvalidShape = false
  LinkTransform = true
  LinkedObject = -> Assembly001 [1.$Element102.]
  TreeRank = 660
  ValidateShape = false
  _LinkVersion = 1
  _Parent = -> Elements003
FEATURE [Part::FeaturePython] Element104  # link proxy (typed FeaturePython)
  Detach = false
  InvalidShape = false
  LinkTransform = true
  LinkedObject = -> Link001 [Pad.Edge29]
  TreeRank = 661
  ValidateShape = false
  _LinkVersion = 1
  _Parent = -> Elements001
FEATURE [Part::FeaturePython] Element105  label="HoleM6_4"  # link proxy (typed FeaturePython)
  Detach = false
  InvalidShape = false
  LinkTransform = true
  LinkedObject = -> Assembly001 [1.$Element104.]
  TreeRank = 662
  ValidateShape = false
  _LinkVersion = 1
  _Parent = -> Elements003
FEATURE [Part::FeaturePython] Element106  # link proxy (typed FeaturePython)
  Detach = false
  InvalidShape = false
  LinkTransform = true
  LinkedObject = -> Link002 [Chamfer001.Edge35]
  TreeRank = 672
  ValidateShape = false
  _LinkVersion = 1
  _Parent = -> Elements002
FEATURE [Part::FeaturePython] Element107  label="HoleM6_5"  # link proxy (typed FeaturePython)
  Detach = false
  InvalidShape = false
  LinkTransform = true
  LinkedObject = -> Assembly002 [1.$Element106.]
  TreeRank = 673
  ValidateShape = false
  _LinkVersion = 1
  _Parent = -> Elements003
FEATURE [Part::FeaturePython] Element108  # link proxy (typed FeaturePython)
  Detach = false
  InvalidShape = false
  LinkTransform = true
  LinkedObject = -> Link002 [Chamfer001.Edge37]
  TreeRank = 674
  ValidateShape = false
  _LinkVersion = 1
  _Parent = -> Elements002
FEATURE [Part::FeaturePython] Element109  label="HoleM6_6"  # link proxy (typed FeaturePython)
  Detach = false
  InvalidShape = false
  LinkTransform = true
  LinkedObject = -> Assembly002 [1.$Element108.]
  TreeRank = 675
  ValidateShape = false
  _LinkVersion = 1
  _Parent = -> Elements003
FEATURE [Part::FeaturePython] Element110  # link proxy (typed FeaturePython)
  Detach = false
  InvalidShape = false
  LinkTransform = true
  LinkedObject = -> Link002 [Chamfer001.Edge36]
  TreeRank = 676
  ValidateShape = false
  _LinkVersion = 1
  _Parent = -> Elements002
FEATURE [Part::FeaturePython] Element111  label="HoleM6_7"  # link proxy (typed FeaturePython)
  Detach = false
  InvalidShape = false
  LinkTransform = true
  LinkedObject = -> Assembly002 [1.$Element110.]
  TreeRank = 677
  ValidateShape = false
  _LinkVersion = 1
  _Parent = -> Elements003
FEATURE [Part::FeaturePython] Element112  # link proxy (typed FeaturePython)
  Detach = false
  InvalidShape = false
  LinkTransform = true
  LinkedObject = -> Link002 [Chamfer001.Edge34]
  TreeRank = 678
  ValidateShape = false
  _LinkVersion = 1
  _Parent = -> Elements002
FEATURE [Part::FeaturePython] Element113  label="HoleM6_8"  # link proxy (typed FeaturePython)
  Detach = false
  InvalidShape = false
  LinkTransform = true
  LinkedObject = -> Assembly002 [1.$Element112.]
  TreeRank = 679
  ValidateShape = false
  _LinkVersion = 1
  _Parent = -> Elements003
FEATURE [Part::FeaturePython] Element114  # WARN: FeaturePython — macro-defined, semantics opaque (R4)
  Detach = false
  InvalidShape = false
  LinkTransform = true
  TreeRank = 700
  ValidateShape = false
  _LinkVersion = 1
  _Parent = -> Elements003
FEATURE [App::FeaturePython] Constraint060  label="Attachment025"  # WARN: FeaturePython — macro-defined, semantics opaque (R4)
  Cascade = false
  Disabled = false
  Group = -> [ElementLink128,ElementLink129]
  Multiply = false
  TreeRank = 744
  _ConstraintType = 45
  _LinkVersion = 1
  _Parent = -> Constraints002
FEATURE [App::FeaturePython] ElementLink128  label="М5_12_посадка@М5х12@#0"  # link proxy (typed FeaturePython)
  LinkTransform = true
  LinkedObject = -> _Element056
  Offset = pos=(0,0,0) rot=(1,0,0;3.14159rad)
  Placement = pos=(-2.84e-14,828.154,529.6) rot=(1,0,0;3.14159rad)
  TreeRank = 745
  _LinkVersion = 1
  _Parent = -> Constraint060
FEATURE [App::FeaturePython] ElementLink129  label="1_plate"  # link proxy (typed FeaturePython)
  LinkTransform = true
  LinkedObject = -> Element021
  TreeRank = 746
  _LinkVersion = 1
  _Parent = -> Constraint060
FEATURE [App::FeaturePython] Constraint061  label="Attachment026"  # WARN: FeaturePython — macro-defined, semantics opaque (R4)
  Cascade = false
  Disabled = false
  Group = -> [ElementLink130,ElementLink131]
  Multiply = false
  TreeRank = 747
  _ConstraintType = 45
  _LinkVersion = 1
  _Parent = -> Constraints002
FEATURE [App::FeaturePython] ElementLink130  label="М5_12_посадка@М5х12@#1"  # link proxy (typed FeaturePython)
  LinkTransform = true
  LinkedObject = -> _Element057
  Offset = pos=(0,0,0) rot=(1,0,0;3.14159rad)
  Placement = pos=(0,733.874,529.6) rot=(1,0,0;3.14159rad)
  TreeRank = 748
  _LinkVersion = 1
  _Parent = -> Constraint061
FEATURE [App::FeaturePython] ElementLink131  label="2_plate"  # link proxy (typed FeaturePython)
  LinkTransform = true
  LinkedObject = -> Element020
  TreeRank = 749
  _LinkVersion = 1
  _Parent = -> Constraint061
FEATURE [App::FeaturePython] Constraint062  label="Attachment027"  # WARN: FeaturePython — macro-defined, semantics opaque (R4)
  Cascade = false
  Disabled = false
  Group = -> [ElementLink132,ElementLink133]
  Multiply = false
  TreeRank = 750
  _ConstraintType = 45
  _LinkVersion = 1
  _Parent = -> Constraints002
FEATURE [App::FeaturePython] ElementLink132  label="М5_12_посадка@М5х12@#2"  # link proxy (typed FeaturePython)
  LinkTransform = true
  LinkedObject = -> _Element058
  Offset = pos=(0,0,0) rot=(1,0,0;3.14159rad)
  Placement = pos=(2.84e-14,733.874,529.6) rot=(1,0,0;3.14159rad)
  TreeRank = 751
  _LinkVersion = 1
  _Parent = -> Constraint062
FEATURE [App::FeaturePython] ElementLink133  label="3_plate"  # link proxy (typed FeaturePython)
  LinkTransform = true
  LinkedObject = -> Element022
  TreeRank = 752
  _LinkVersion = 1
  _Parent = -> Constraint062
FEATURE [App::FeaturePython] Constraint063  label="Attachment028"  # WARN: FeaturePython — macro-defined, semantics opaque (R4)
  Cascade = false
  Disabled = false
  Group = -> [ElementLink134,ElementLink135]
  Multiply = false
  TreeRank = 753
  _ConstraintType = 45
  _LinkVersion = 1
  _Parent = -> Constraints002
FEATURE [App::FeaturePython] ElementLink134  label="М5_12_посадка@М5х12@#3"  # link proxy (typed FeaturePython)
  LinkTransform = true
  LinkedObject = -> _Element059
  Offset = pos=(0,0,0) rot=(1,0,0;3.14159rad)
  Placement = pos=(-2.84e-14,828.154,529.6) rot=(1,0,0;3.14159rad)
  TreeRank = 754
  _LinkVersion = 1
  _Parent = -> Constraint063
FEATURE [App::FeaturePython] ElementLink135  label="4_plate"  # link proxy (typed FeaturePython)
  LinkTransform = true
  LinkedObject = -> Element023
  TreeRank = 755
  _LinkVersion = 1
  _Parent = -> Constraint063
FEATURE [Part::FeaturePython] _Element022  # link proxy (typed FeaturePython)
  Detach = false
  InvalidShape = false
  LinkTransform = true
  LinkedObject = -> Link012 [LinearPattern.?Face5]
  TreeRank = 756
  ValidateShape = false
  _LinkVersion = 1
  _Parent = -> Elements004
FEATURE [App::FeaturePython] Constraint064  label="Locked005"  # WARN: FeaturePython — macro-defined, semantics opaque (R4)
  Disabled = false
  Group = -> [ElementLink137]
  TreeRank = 759
  _ConstraintType = 0
  _LinkVersion = 1
  _Parent = -> Constraints004
FEATURE [App::FeaturePython] ElementLink137  label="_Element022"  # link proxy (typed FeaturePython)
  LinkTransform = true
  LinkedObject = -> _Element022
  TreeRank = 760
  _LinkVersion = 1
  _Parent = -> Constraint064
FEATURE [Part::FeaturePython] _Element049  label="ЛПлЛВ@СборкаЗащита@"  # link proxy (typed FeaturePython)
  Detach = false
  InvalidShape = false
  LinkTransform = true
  LinkedObject = -> Assembly004 [1.$ЛПлЛВ.]
  TreeRank = 824
  ValidateShape = false
  _LinkVersion = 1
  _Parent = -> Elements003
FEATURE [Part::FeaturePython] Element143  label="ЛвШайбВерх@Ролики@#0"  # link proxy (typed FeaturePython)
  Detach = false
  InvalidShape = false
  LinkTransform = true
  LinkedObject = -> Link014 [Link014_i0.1.$ЛвШайбВерх.]
  TreeRank = 826
  ValidateShape = false
  _LinkVersion = 1
  _Parent = -> Elements004
FEATURE [Part::FeaturePython] _Element050  label="ЛвШайбВерх@СборкаЗащита@#0"  # link proxy (typed FeaturePython)
  Detach = false
  InvalidShape = false
  LinkTransform = true
  LinkedObject = -> Assembly004 [1.$ЛвШайбВерх@Ролики@#0.]
  TreeRank = 827
  ValidateShape = false
  _LinkVersion = 1
  _Parent = -> Elements003
FEATURE [App::FeaturePython] Constraint074  label="Attachment038"  # WARN: FeaturePython — macro-defined, semantics opaque (R4)
  Cascade = false
  Disabled = false
  Group = -> [ElementLink156,ElementLink157]
  Multiply = false
  TreeRank = 832
  _ConstraintType = 45
  _LinkVersion = 1
  _Parent = -> Constraints004
FEATURE [App::FeaturePython] ElementLink156  label="ПрШайбВерх@Ролики@#0"  # link proxy (typed FeaturePython)
  LinkTransform = true
  LinkedObject = -> _Element051
  TreeRank = 829
  _LinkVersion = 1
  _Parent = -> Constraint074
FEATURE [Part::FeaturePython] _Element051  label="ПрШайбВерх@Ролики@#0"  # link proxy (typed FeaturePython)
  Detach = false
  InvalidShape = false
  LinkTransform = true
  LinkedObject = -> Link014 [Link014_i0.1.$ПрШайбВерх.]
  TreeRank = 833
  ValidateShape = false
  _LinkVersion = 1
  _Parent = -> Elements004
FEATURE [App::FeaturePython] ElementLink157  label="ЛПлЛВ"  # link proxy (typed FeaturePython)
  LinkTransform = true
  LinkedObject = -> Element052
  TreeRank = 831
  _LinkVersion = 1
  _Parent = -> Constraint074
FEATURE [Part::FeaturePython] _Element052  label="ЛвГайкаНиз@Ролики@#1"  # link proxy (typed FeaturePython)
  Detach = false
  InvalidShape = false
  LinkTransform = true
  LinkedObject = -> Link014 [Link014_i1.1.$ЛвГайкаНиз.]
  TreeRank = 837
  ValidateShape = false
  _LinkVersion = 1
  _Parent = -> Elements004
FEATURE [App::FeaturePython] Constraint075  label="Attachment039"  # WARN: FeaturePython — macro-defined, semantics opaque (R4)
  Cascade = false
  Disabled = false
  Group = -> [ElementLink158,ElementLink159]
  Multiply = false
  TreeRank = 838
  _ConstraintType = 45
  _LinkVersion = 1
  _Parent = -> Constraints004
FEATURE [App::FeaturePython] ElementLink158  label="ЛПлЛН"  # link proxy (typed FeaturePython)
  LinkTransform = true
  LinkedObject = -> Element053
  TreeRank = 839
  _LinkVersion = 1
  _Parent = -> Constraint075
FEATURE [App::FeaturePython] ElementLink159  label="ЛвШайбВерх@Ролики@#1"  # link proxy (typed FeaturePython)
  LinkTransform = true
  LinkedObject = -> _Element053
  TreeRank = 840
  _LinkVersion = 1
  _Parent = -> Constraint075
FEATURE [Part::FeaturePython] _Element053  label="ЛвШайбВерх@Ролики@#1"  # link proxy (typed FeaturePython)
  Detach = false
  InvalidShape = false
  LinkTransform = true
  LinkedObject = -> Link014 [Link014_i1.1.$ЛвШайбВерх.]
  TreeRank = 841
  ValidateShape = false
  _LinkVersion = 1
  _Parent = -> Elements004
FEATURE [App::FeaturePython] Constraint076  label="Attachment040"  # WARN: FeaturePython — macro-defined, semantics opaque (R4)
  Cascade = false
  Disabled = false
  Group = -> [ElementLink160,ElementLink161]
  Multiply = false
  TreeRank = 842
  _ConstraintType = 45
  _LinkVersion = 1
  _Parent = -> Constraints004
FEATURE [App::FeaturePython] ElementLink160  label="ПрШайбВерх@Ролики@#2"  # link proxy (typed FeaturePython)
  LinkTransform = true
  LinkedObject = -> _Element054
  TreeRank = 843
  _LinkVersion = 1
  _Parent = -> Constraint076
FEATURE [Part::FeaturePython] _Element054  label="ПрШайбВерх@Ролики@#2"  # link proxy (typed FeaturePython)
  Detach = false
  InvalidShape = false
  LinkTransform = true
  LinkedObject = -> Link014 [Link014_i2.1.$ПрШайбВерх.]
  TreeRank = 844
  ValidateShape = false
  _LinkVersion = 1
  _Parent = -> Elements004
FEATURE [App::FeaturePython] ElementLink161  label="ЛПлПВ"  # link proxy (typed FeaturePython)
  LinkTransform = true
  LinkedObject = -> Element054
  TreeRank = 845
  _LinkVersion = 1
  _Parent = -> Constraint076
FEATURE [App::FeaturePython] Constraint077  label="Attachment041"  # WARN: FeaturePython — macro-defined, semantics opaque (R4)
  Cascade = false
  Disabled = false
  Group = -> [ElementLink162,ElementLink163]
  Multiply = false
  TreeRank = 846
  _ConstraintType = 45
  _LinkVersion = 1
  _Parent = -> Constraints004
FEATURE [App::FeaturePython] ElementLink162  label="ПрШайбВерх@Ролики@#3"  # link proxy (typed FeaturePython)
  LinkTransform = true
  LinkedObject = -> _Element055
  TreeRank = 847
  _LinkVersion = 1
  _Parent = -> Constraint077
FEATURE [Part::FeaturePython] _Element055  label="ПрШайбВерх@Ролики@#3"  # link proxy (typed FeaturePython)
  Detach = false
  InvalidShape = false
  LinkTransform = true
  LinkedObject = -> Link014 [Link014_i3.1.$ПрШайбВерх.]
  TreeRank = 848
  ValidateShape = false
  _LinkVersion = 1
  _Parent = -> Elements004
FEATURE [App::FeaturePython] ElementLink163  label="ЛПлПН"  # link proxy (typed FeaturePython)
  LinkTransform = true
  LinkedObject = -> Element055
  TreeRank = 849
  _LinkVersion = 1
  _Parent = -> Constraint077
FEATURE [App::FeaturePython] Constraint078  label="Attachment042"  # WARN: FeaturePython — macro-defined, semantics opaque (R4)
  Cascade = false
  Disabled = false
  Group = -> [ElementLink165,ElementLink166]
  Multiply = false
  TreeRank = 854
  _ConstraintType = 45
  _LinkVersion = 1
  _Parent = -> Constraints004
FEATURE [App::FeaturePython] ElementLink165  label="ППлЛВ"  # link proxy (typed FeaturePython)
  LinkTransform = true
  LinkedObject = -> Element056
  Offset = pos=(0,0,0) rot=(1,0,0;3.14159rad)
  Placement = pos=(2.558e-13,82,446.6) rot=(1,0,0;3.14159rad)
  TreeRank = 855
  _LinkVersion = 1
  _Parent = -> Constraint078
FEATURE [App::FeaturePython] ElementLink166  label="ЛвШайбВерх@Ролики@#0"  # link proxy (typed FeaturePython)
  LinkTransform = true
  LinkedObject = -> Element143
  TreeRank = 856
  _LinkVersion = 1
  _Parent = -> Constraint078
FEATURE [Part::FeaturePython] Element144  label="Винт@КрепежМ6_Тгайка@#0"  # link proxy (typed FeaturePython)
  Detach = false
  InvalidShape = false
  LinkTransform = true
  LinkedObject = -> Link030 [Link030_i0.1.$Винт.]
  TreeRank = 875
  ValidateShape = false
  _LinkVersion = 1
  _Parent = -> Elements003
FEATURE [Part::FeaturePython] Element145  label="Винт@КрепежМ6_Тгайка@#1"  # link proxy (typed FeaturePython)
  Detach = false
  InvalidShape = false
  LinkTransform = true
  LinkedObject = -> Link030 [Link030_i1.1.$Винт.]
  TreeRank = 876
  ValidateShape = false
  _LinkVersion = 1
  _Parent = -> Elements003
FEATURE [Part::FeaturePython] Element146  label="Винт@КрепежМ6_Тгайка@#2"  # link proxy (typed FeaturePython)
  Detach = false
  InvalidShape = false
  LinkTransform = true
  LinkedObject = -> Link030 [Link030_i2.1.$Винт.]
  TreeRank = 877
  ValidateShape = false
  _LinkVersion = 1
  _Parent = -> Elements003
FEATURE [Part::FeaturePython] Element147  label="Винт@КрепежМ6_Тгайка@#3"  # link proxy (typed FeaturePython)
  Detach = false
  InvalidShape = false
  LinkTransform = true
  LinkedObject = -> Link030 [Link030_i3.1.$Винт.]
  TreeRank = 878
  ValidateShape = false
  _LinkVersion = 1
  _Parent = -> Elements003
FEATURE [Part::FeaturePython] Element148  label="Винт@КрепежМ6_Тгайка@#4"  # link proxy (typed FeaturePython)
  Detach = false
  InvalidShape = false
  LinkTransform = true
  LinkedObject = -> Link030 [Link030_i4.1.$Винт.]
  TreeRank = 879
  ValidateShape = false
  _LinkVersion = 1
  _Parent = -> Elements003
FEATURE [Part::FeaturePython] Element149  label="Винт@КрепежМ6_Тгайка@#5"  # link proxy (typed FeaturePython)
  Detach = false
  InvalidShape = false
  LinkTransform = true
  LinkedObject = -> Link030 [Link030_i5.1.$Винт.]
  TreeRank = 880
  ValidateShape = false
  _LinkVersion = 1
  _Parent = -> Elements003
FEATURE [Part::FeaturePython] Element150  label="Винт@КрепежМ6_Тгайка@#6"  # link proxy (typed FeaturePython)
  Detach = false
  InvalidShape = false
  LinkTransform = true
  LinkedObject = -> Link030 [Link030_i6.1.$Винт.]
  TreeRank = 881
  ValidateShape = false
  _LinkVersion = 1
  _Parent = -> Elements003
FEATURE [Part::FeaturePython] Element151  label="Винт@КрепежМ6_Тгайка@#7"  # link proxy (typed FeaturePython)
  Detach = false
  InvalidShape = false
  LinkTransform = true
  LinkedObject = -> Link030 [Link030_i7.1.$Винт.]
  TreeRank = 882
  ValidateShape = false
  _LinkVersion = 1
  _Parent = -> Elements003
FEATURE [App::FeaturePython] Constraint079  label="Attachment043"  # WARN: FeaturePython — macro-defined, semantics opaque (R4)
  Cascade = false
  Disabled = false
  Group = -> [ElementLink167,ElementLink168]
  Multiply = false
  TreeRank = 884
  _ConstraintType = 45
  _LinkVersion = 1
  _Parent = -> Constraints003
FEATURE [App::FeaturePython] ElementLink167  label="HoleM6_1"  # link proxy (typed FeaturePython)
  LinkTransform = true
  LinkedObject = -> Element099
  TreeRank = 885
  _LinkVersion = 1
  _Parent = -> Constraint079
FEATURE [App::FeaturePython] ElementLink168  label="Винт@КрепежМ6_Тгайка@#0"  # link proxy (typed FeaturePython)
  LinkTransform = true
  LinkedObject = -> Element144
  TreeRank = 886
  _LinkVersion = 1
  _Parent = -> Constraint079
FEATURE [App::FeaturePython] Constraint080  label="Attachment044"  # WARN: FeaturePython — macro-defined, semantics opaque (R4)
  Cascade = false
  Disabled = false
  Group = -> [ElementLink169,ElementLink170]
  Multiply = false
  TreeRank = 887
  _ConstraintType = 45
  _LinkVersion = 1
  _Parent = -> Constraints003
FEATURE [App::FeaturePython] ElementLink169  label="HoleM6_2"  # link proxy (typed FeaturePython)
  LinkTransform = true
  LinkedObject = -> Element101
  TreeRank = 888
  _LinkVersion = 1
  _Parent = -> Constraint080
FEATURE [App::FeaturePython] ElementLink170  label="Винт@КрепежМ6_Тгайка@#1"  # link proxy (typed FeaturePython)
  LinkTransform = true
  LinkedObject = -> Element145
  TreeRank = 889
  _LinkVersion = 1
  _Parent = -> Constraint080
FEATURE [App::FeaturePython] Constraint081  label="Attachment045"  # WARN: FeaturePython — macro-defined, semantics opaque (R4)
  Cascade = false
  Disabled = false
  Group = -> [ElementLink171,ElementLink172]
  Multiply = false
  TreeRank = 890
  _ConstraintType = 45
  _LinkVersion = 1
  _Parent = -> Constraints003
FEATURE [App::FeaturePython] ElementLink171  label="HoleM6_3"  # link proxy (typed FeaturePython)
  LinkTransform = true
  LinkedObject = -> Element103
  TreeRank = 891
  _LinkVersion = 1
  _Parent = -> Constraint081
FEATURE [App::FeaturePython] ElementLink172  label="Винт@КрепежМ6_Тгайка@#2"  # link proxy (typed FeaturePython)
  LinkTransform = true
  LinkedObject = -> Element146
  TreeRank = 892
  _LinkVersion = 1
  _Parent = -> Constraint081
FEATURE [App::FeaturePython] Constraint082  label="Attachment046"  # WARN: FeaturePython — macro-defined, semantics opaque (R4)
  Cascade = false
  Disabled = false
  Group = -> [ElementLink173,ElementLink174]
  Multiply = false
  TreeRank = 893
  _ConstraintType = 45
  _LinkVersion = 1
  _Parent = -> Constraints003
FEATURE [App::FeaturePython] ElementLink173  label="HoleM6_4"  # link proxy (typed FeaturePython)
  LinkTransform = true
  LinkedObject = -> Element105
  TreeRank = 894
  _LinkVersion = 1
  _Parent = -> Constraint082
FEATURE [App::FeaturePython] ElementLink174  label="Винт@КрепежМ6_Тгайка@#3"  # link proxy (typed FeaturePython)
  LinkTransform = true
  LinkedObject = -> Element147
  TreeRank = 895
  _LinkVersion = 1
  _Parent = -> Constraint082
FEATURE [App::FeaturePython] Constraint083  label="Attachment047"  # WARN: FeaturePython — macro-defined, semantics opaque (R4)
  Cascade = false
  Disabled = false
  Group = -> [ElementLink175,ElementLink176]
  Multiply = false
  TreeRank = 896
  _ConstraintType = 45
  _LinkVersion = 1
  _Parent = -> Constraints003
FEATURE [App::FeaturePython] ElementLink175  label="HoleM6_5"  # link proxy (typed FeaturePython)
  LinkTransform = true
  LinkedObject = -> Element107
  TreeRank = 897
  _LinkVersion = 1
  _Parent = -> Constraint083
FEATURE [App::FeaturePython] ElementLink176  label="Винт@КрепежМ6_Тгайка@#4"  # link proxy (typed FeaturePython)
  LinkTransform = true
  LinkedObject = -> Element148
  TreeRank = 898
  _LinkVersion = 1
  _Parent = -> Constraint083
FEATURE [App::FeaturePython] Constraint084  label="Attachment048"  # WARN: FeaturePython — macro-defined, semantics opaque (R4)
  Cascade = false
  Disabled = false
  Group = -> [ElementLink177,ElementLink178]
  Multiply = false
  TreeRank = 899
  _ConstraintType = 45
  _LinkVersion = 1
  _Parent = -> Constraints003
FEATURE [App::FeaturePython] ElementLink177  label="HoleM6_6"  # link proxy (typed FeaturePython)
  LinkTransform = true
  LinkedObject = -> Element109
  TreeRank = 900
  _LinkVersion = 1
  _Parent = -> Constraint084
FEATURE [App::FeaturePython] ElementLink178  label="Винт@КрепежМ6_Тгайка@#5"  # link proxy (typed FeaturePython)
  LinkTransform = true
  LinkedObject = -> Element149
  TreeRank = 901
  _LinkVersion = 1
  _Parent = -> Constraint084
FEATURE [App::FeaturePython] Constraint085  label="Attachment049"  # WARN: FeaturePython — macro-defined, semantics opaque (R4)
  Cascade = false
  Disabled = false
  Group = -> [ElementLink179,ElementLink180]
  Multiply = false
  TreeRank = 902
  _ConstraintType = 45
  _LinkVersion = 1
  _Parent = -> Constraints003
FEATURE [App::FeaturePython] ElementLink179  label="HoleM6_7"  # link proxy (typed FeaturePython)
  LinkTransform = true
  LinkedObject = -> Element111
  TreeRank = 903
  _LinkVersion = 1
  _Parent = -> Constraint085
FEATURE [App::FeaturePython] ElementLink180  label="Винт@КрепежМ6_Тгайка@#6"  # link proxy (typed FeaturePython)
  LinkTransform = true
  LinkedObject = -> Element150
  TreeRank = 904
  _LinkVersion = 1
  _Parent = -> Constraint085
FEATURE [App::FeaturePython] Constraint086  label="Attachment050"  # WARN: FeaturePython — macro-defined, semantics opaque (R4)
  Cascade = false
  Disabled = false
  Group = -> [ElementLink181,ElementLink182]
  Multiply = false
  TreeRank = 905
  _ConstraintType = 45
  _LinkVersion = 1
  _Parent = -> Constraints003
FEATURE [App::FeaturePython] ElementLink181  label="HoleM6_8"  # link proxy (typed FeaturePython)
  LinkTransform = true
  LinkedObject = -> Element113
  TreeRank = 906
  _LinkVersion = 1
  _Parent = -> Constraint086
FEATURE [App::FeaturePython] ElementLink182  label="Винт@КрепежМ6_Тгайка@#7"  # link proxy (typed FeaturePython)
  LinkTransform = true
  LinkedObject = -> Element151
  TreeRank = 907
  _LinkVersion = 1
  _Parent = -> Constraint086
FEATURE [Part::FeaturePython] _Element056  label="М5_12_посадка@М5х12@#0"  # link proxy (typed FeaturePython)
  Detach = false
  InvalidShape = false
  LinkTransform = true
  LinkedObject = -> Link031 [Link031_i0.1.$М5_12_посадка.]
  TreeRank = 913
  ValidateShape = false
  _LinkVersion = 1
  _Parent = -> Elements002
FEATURE [Part::FeaturePython] _Element057  label="М5_12_посадка@М5х12@#1"  # link proxy (typed FeaturePython)
  Detach = false
  InvalidShape = false
  LinkTransform = true
  LinkedObject = -> Link031 [Link031_i1.1.$М5_12_посадка.]
  TreeRank = 914
  ValidateShape = false
  _LinkVersion = 1
  _Parent = -> Elements002
FEATURE [Part::FeaturePython] _Element058  label="М5_12_посадка@М5х12@#2"  # link proxy (typed FeaturePython)
  Detach = false
  InvalidShape = false
  LinkTransform = true
  LinkedObject = -> Link031 [Link031_i2.1.$М5_12_посадка.]
  TreeRank = 915
  ValidateShape = false
  _LinkVersion = 1
  _Parent = -> Elements002
FEATURE [Part::FeaturePython] _Element059  label="М5_12_посадка@М5х12@#3"  # link proxy (typed FeaturePython)
  Detach = false
  InvalidShape = false
  LinkTransform = true
  LinkedObject = -> Link031 [Link031_i3.1.$М5_12_посадка.]
  TreeRank = 916
  ValidateShape = false
  _LinkVersion = 1
  _Parent = -> Elements002
FEATURE [Part::FeaturePython] _Element060  label="М4_16_посадка@М4х16@#0"  # link proxy (typed FeaturePython)
  Detach = false
  InvalidShape = false
  LinkTransform = true
  LinkedObject = -> Link032 [Link032_i0.1.$М4_16_посадка.]
  TreeRank = 922
  ValidateShape = false
  _LinkVersion = 1
  _Parent = -> Elements001
FEATURE [Part::FeaturePython] _Element061  label="М4_16_посадка@М4х16@#1"  # link proxy (typed FeaturePython)
  Detach = false
  InvalidShape = false
  LinkTransform = true
  LinkedObject = -> Link032 [Link032_i1.1.$М4_16_посадка.]
  TreeRank = 923
  ValidateShape = false
  _LinkVersion = 1
  _Parent = -> Elements001
FEATURE [Part::FeaturePython] _Element062  label="М4_16_посадка@М4х16@#2"  # link proxy (typed FeaturePython)
  Detach = false
  InvalidShape = false
  LinkTransform = true
  LinkedObject = -> Link032 [Link032_i2.1.$М4_16_посадка.]
  TreeRank = 924
  ValidateShape = false
  _LinkVersion = 1
  _Parent = -> Elements001
FEATURE [Part::FeaturePython] _Element063  label="М4_16_посадка@М4х16@#3"  # link proxy (typed FeaturePython)
  Detach = false
  InvalidShape = false
  LinkTransform = true
  LinkedObject = -> Link032 [Link032_i3.1.$М4_16_посадка.]
  TreeRank = 925
  ValidateShape = false
  _LinkVersion = 1
  _Parent = -> Elements001
FEATURE [Part::FeaturePython] Element152  # link proxy (typed FeaturePython)
  Detach = false
  InvalidShape = false
  LinkTransform = true
  LinkedObject = -> Assembly002 [1.$Element037.]
  TreeRank = 926
  ValidateShape = false
  _LinkVersion = 1
  _Parent = -> Elements003
FEATURE [Part::FeaturePython] Element154  # WARN: FeaturePython — macro-defined, semantics opaque (R4)
  Detach = false
  InvalidShape = false
  LinkTransform = true
  TreeRank = 928
  ValidateShape = false
  _LinkVersion = 1
  _Parent = -> Elements003
FEATURE [Part::FeaturePython] Element155  # link proxy (typed FeaturePython)
  Detach = false
  InvalidShape = false
  LinkTransform = true
  LinkedObject = -> Link013 [LinearPattern.Edge40]
  TreeRank = 929
  ValidateShape = false
  _LinkVersion = 1
  _Parent = -> Elements004
FEATURE [Part::FeaturePython] Element156  # link proxy (typed FeaturePython)
  Detach = false
  InvalidShape = false
  LinkTransform = true
  LinkedObject = -> Assembly004 [1.$Element155.]
  TreeRank = 930
  ValidateShape = false
  _LinkVersion = 1
  _Parent = -> Elements003
FEATURE [Part::FeaturePython] Element157  # link proxy (typed FeaturePython)
  Detach = false
  InvalidShape = false
  LinkTransform = true
  LinkedObject = -> Link012 [LinearPattern.Edge18]
  TreeRank = 931
  ValidateShape = false
  _LinkVersion = 1
  _Parent = -> Elements004
FEATURE [Part::FeaturePython] Element158  # link proxy (typed FeaturePython)
  Detach = false
  InvalidShape = false
  LinkTransform = true
  LinkedObject = -> Assembly004 [1.$Element157.]
  TreeRank = 932
  ValidateShape = false
  _LinkVersion = 1
  _Parent = -> Elements003

RESOLVED EXTERNAL PARTS (link-assembly join: the EXTERNAL_REF files above that resolve inside this repo's crawl, each included once):
---- part Крепеж.FCStd = doc fcstd_4da76f0b1cb2 ----
FCSTD DOCUMENT  (FreeCAD 0.20R30972 (Git))
Label: Крепеж
License: All rights reserved
LicenseURL: http://en.wikipedia.org/wiki/All_rights_reserved
objects: Part::FeaturePython×14, App::FeaturePython×9, Sketcher::SketchObject×7, PartDesign::Pad×4, PartDesign::Hole×4, PartDesign::Body×4, App::Link×1
note: 46 computed .brp shape members not serialized (recipe doc carries the construction recipe); baked Part::Feature solids carry a one-line shape summary decoded from their .brp
EXTERNAL_REF file=ТаблицаПараметров.FCStd obj=Spreadsheet002

FEATURE [Sketcher::SketchObject] Sketch004
  FullyConstrained = true
  MapMode = 2
  TreeRank = 11
  sketch-geometry (10):
    g0: LineSegment StartX=-5 StartY=3 StartZ=0 EndX=5 EndY=3 EndZ=0
    g1: LineSegment StartX=5 StartY=3 StartZ=0 EndX=8 EndY=0 EndZ=0
    g2: LineSegment StartX=8 StartY=0 StartZ=0 EndX=8 EndY=-1.2 EndZ=0
    g3: LineSegment StartX=8 StartY=-1.2 StartZ=0 EndX=3.9 EndY=-1.2 EndZ=0
    g4: LineSegment StartX=3.9 StartY=-1.2 StartZ=0 EndX=3.9 EndY=-3 EndZ=0
    g5: LineSegment StartX=3.9 StartY=-3 StartZ=0 EndX=-3.9 EndY=-3 EndZ=0
    g6: LineSegment StartX=-3.9 StartY=-3 StartZ=0 EndX=-3.9 EndY=-1.2 EndZ=0
    g7: LineSegment StartX=-3.9 StartY=-1.2 StartZ=0 EndX=-8 EndY=-1.2 EndZ=0
    g8: LineSegment StartX=-8 StartY=-1.2 StartZ=0 EndX=-8 EndY=0 EndZ=0
    g9: LineSegment StartX=-8 StartY=0 StartZ=0 EndX=-5 EndY=3 EndZ=0
  constraints (28):
    c: PointOnObject(g1,g-1)
    c: Vertical(g2)
    c: Coincident(g3,g2)
    c: Horizontal(g3)
    c: Coincident(g4,g3)
    c: Coincident(g6,g5)
    c: Coincident(g7,g6)
    c: Horizontal(g7)
    c: Coincident(g8,g7)
    c: PointOnObject(g8,g-1)
    c: Vertical(g8)
    c: Coincident(g9,g0)
    c: Coincident(g0,g1)
    c: Coincident(g1,g2)
    c: Coincident(g5,g4)
    c: Vertical(g4)
    c: Vertical(g6)
    c: DistanceX(g0,g0) = 10
    c: Angle(g-1,g9) = 0.785398
    c: Coincident(g9,g8)
    c: Angle(g1,g-1) = 0.785398
    c: Symmetric(g0,g0,g-2)
    c: DistanceX(g5,g5) = 7.8
    c: Symmetric(g5,g4,g-2)
    c: DistanceY(g4,g4) = 1.8
    c: DistanceX(g7,g2) = 16
    c: DistanceY(g6,g6) = 1.8
    c: DistanceY(g5,g0) = 6
FEATURE [PartDesign::Pad] Pad002
  AddSubType = 0
  AlongSketchNormal = false
  CheckUpToFaceLimits = true
  ClaimChildren = false
  Direction = (0,0,1)
  Fit = 0
  FitJoin = 0
  InnerFit = 0
  InnerFitJoin = 0
  InnerTaperAngle = 0
  InnerTaperAngleRev = 0
  Length = 16
  Length2 = 100
  Linearize = true
  NewSolid = false
  Profile = -> Sketch004
  Suppress = false
  TreeRank = 12
  Type = 0
  _ProfileBasedVersion = 1
FEATURE [Sketcher::SketchObject] Sketch005
  FullyConstrained = true
  MapMode = 5
  Placement = pos=(0,-3,0) rot=(1,0,0;1.5708rad)
  Support = -> [Pad002]
  TreeRank = 13
  sketch-geometry (1):
    g0: Circle CenterX=0 CenterY=8 CenterZ=0 NormalX=0 NormalY=0 NormalZ=1 AngleXU=0 Radius=1.6
  constraints (3):
    c: PointOnObject(g0,g-2)
    c: DistanceY(g-1,g0) = 8
    c: Diameter(g0) = 3.2
FEATURE [PartDesign::Hole] Hole002
  AddSubType = 1
  BaseFeature = -> Pad002
  ClaimChildren = false
  CustomThreadClearance = 0
  Depth = 6
  DepthType = 0
  Diameter = 6.6
  DrillForDepth = false
  DrillPoint = 1
  DrillPointAngle = 118
  Fit = 0
  FitJoin = 0
  HoleCutCountersinkAngle = 90
  HoleCutCustomValues = false
  HoleCutDepth = 0
  HoleCutDiameter = 6.1
  HoleCutType = 0
  InnerFit = 0
  InnerFitJoin = 0
  Linearize = true
  ModelThread = true
  NewSolid = false
  Profile = -> Sketch005
  Suppress = false
  Tapered = false
  TaperedAngle = 90
  ThreadClass = 0
  ThreadDepth = 6
  ThreadDepthType = 1
  ThreadDirection = 0
  ThreadFit = 0
  ThreadSize = 14
  ThreadType = 1
  Threaded = false
  TreeRank = 14
  UseCustomThreadClearance = false
  _ProfileBasedVersion = 1
FEATURE [PartDesign::Body] Body002  label="M6T_nut"
  AutoGroupSolids = false
  ClaimAllChildren = false
  ExportMode = 0
  Group = -> [Sketch004,Pad002,Sketch005,Hole002]
  Origin = -> Origin002
  Tip = -> Hole002
  TreeRank = 777
  _ExportChildren = -> [Pad002,Hole002]
  _GroupVersion = 1
FEATURE [App::Link] Link028  label="M6T_nut_1"
  AutoLinkLabel = true
  AutoPlacement = true
  LinkPlacement = pos=(8,-2.7e-15,16.25) rot=(0.57735,-0.57735,-0.57735;2.0944rad)
  LinkedObject = -> Body002
  Placement = pos=(8,-2.7e-15,16.25) rot=(0.57735,-0.57735,-0.57735;2.0944rad)
  SyncGroupVisibility = false
  TreeRank = 692
  _LinkVersion = 1
FEATURE [Part::FeaturePython] Screw002  label="M6x20-Screw"  # Fasteners workbench fastener (typed FeaturePython)
  Placement = pos=(0,0,0) rot=(1,0,0;3.14159rad)
  TreeRank = 200
  diameter = 7
  invert = false
  length = 5
  lengthCustom = 20
  matchOuter = false
  offset = 0
  thread = false
  type = 34
FEATURE [Part::FeaturePython] Parts005  # WARN: FeaturePython — macro-defined, semantics opaque (R4)
  Group = -> [Link028,Screw002]
  GroupMode = 0
  TreeRank = 764
  _LinkVersion = 1
FEATURE [Sketcher::SketchObject] Sketch
  FullyConstrained = true
  MapMode = 2
  TreeRank = 11
  sketch-geometry (10):
    g0: LineSegment StartX=-5 StartY=3 StartZ=0 EndX=5 EndY=3 EndZ=0
    g1: LineSegment StartX=5 StartY=3 StartZ=0 EndX=8 EndY=0 EndZ=0
    g2: LineSegment StartX=8 StartY=0 StartZ=0 EndX=8 EndY=-1.2 EndZ=0
    g3: LineSegment StartX=8 StartY=-1.2 StartZ=0 EndX=3.9 EndY=-1.2 EndZ=0
    g4: LineSegment StartX=3.9 StartY=-1.2 StartZ=0 EndX=3.9 EndY=-3 EndZ=0
    g5: LineSegment StartX=3.9 StartY=-3 StartZ=0 EndX=-3.9 EndY=-3 EndZ=0
    g6: LineSegment StartX=-3.9 StartY=-3 StartZ=0 EndX=-3.9 EndY=-1.2 EndZ=0
    g7: LineSegment StartX=-3.9 StartY=-1.2 StartZ=0 EndX=-8 EndY=-1.2 EndZ=0
    g8: LineSegment StartX=-8 StartY=-1.2 StartZ=0 EndX=-8 EndY=0 EndZ=0
    g9: LineSegment StartX=-8 StartY=0 StartZ=0 EndX=-5 EndY=3 EndZ=0
  constraints (28):
    c: PointOnObject(g1,g-1)
    c: Vertical(g2)
    c: Coincident(g3,g2)
    c: Horizontal(g3)
    c: Coincident(g4,g3)
    c: Coincident(g6,g5)
    c: Coincident(g7,g6)
    c: Horizontal(g7)
    c: Coincident(g8,g7)
    c: PointOnObject(g8,g-1)
    c: Vertical(g8)
    c: Coincident(g9,g0)
    c: Coincident(g0,g1)
    c: Coincident(g1,g2)
    c: Coincident(g5,g4)
    c: Vertical(g4)
    c: Vertical(g6)
    c: DistanceX(g0,g0) = 10
    c: Angle(g-1,g9) = 0.785398
    c: Coincident(g9,g8)
    c: Angle(g1,g-1) = 0.785398
    c: Symmetric(g0,g0,g-2)
    c: DistanceX(g5,g5) = 7.8
    c: Symmetric(g5,g4,g-2)
    c: DistanceY(g4,g4) = 1.8
    c: DistanceX(g7,g2) = 16
    c: DistanceY(g6,g6) = 1.8
    c: DistanceY(g5,g0) = 6
FEATURE [PartDesign::Pad] Pad
  AddSubType = 0
  AlongSketchNormal = false
  CheckUpToFaceLimits = true
  ClaimChildren = false
  Direction = (0,0,1)
  Fit = 0
  FitJoin = 0
  InnerFit = 0
  InnerFitJoin = 0
  InnerTaperAngle = 0
  InnerTaperAngleRev = 0
  Length = 16
  Length2 = 100
  Linearize = true
  NewSolid = false
  Profile = -> Sketch
  Suppress = false
  TreeRank = 12
  Type = 0
  _ProfileBasedVersion = 1
FEATURE [Sketcher::SketchObject] Sketch001
  FullyConstrained = true
  MapMode = 5
  Placement = pos=(0,-3,0) rot=(1,0,0;1.5708rad)
  Support = -> [Pad]
  TreeRank = 13
  sketch-geometry (1):
    g0: Circle CenterX=0 CenterY=8 CenterZ=0 NormalX=0 NormalY=0 NormalZ=1 AngleXU=0 Radius=1.6
  constraints (3):
    c: PointOnObject(g0,g-2)
    c: DistanceY(g-1,g0) = 8
    c: Diameter(g0) = 3.2
FEATURE [PartDesign::Hole] Hole
  AddSubType = 1
  BaseFeature = -> Pad
  ClaimChildren = false
  CustomThreadClearance = 0
  Depth = 6
  DepthType = 0
  Diameter = 3.322
  DrillForDepth = false
  DrillPoint = 1
  DrillPointAngle = 118
  Fit = 0
  FitJoin = 0
  HoleCutCountersinkAngle = 90
  HoleCutCustomValues = false
  HoleCutDepth = 0
  HoleCutDiameter = 6.1
  HoleCutType = 0
  InnerFit = 0
  InnerFitJoin = 0
  Linearize = true
  ModelThread = true
  NewSolid = false
  Profile = -> Sketch001
  Suppress = false
  Tapered = false
  TaperedAngle = 90
  ThreadClass = 0
  ThreadDepth = 6
  ThreadDepthType = 1
  ThreadDirection = 0
  ThreadFit = 0
  ThreadSize = 11
  ThreadType = 1
  Threaded = true
  TreeRank = 14
  UseCustomThreadClearance = false
  _ProfileBasedVersion = 1
FEATURE [PartDesign::Body] Body  label="M4T_nut"
  AutoGroupSolids = false
  ClaimAllChildren = false
  ExportMode = 0
  Group = -> [Sketch,Pad,Sketch001,Hole]
  Origin = -> Origin
  Tip = -> Hole
  TreeRank = 779
  _ExportChildren = -> [Pad,Hole]
  _GroupVersion = 1
FEATURE [Sketcher::SketchObject] Sketch002
  FullyConstrained = true
  MapMode = 2
  TreeRank = 11
  sketch-geometry (10):
    g0: LineSegment StartX=-5 StartY=3 StartZ=0 EndX=5 EndY=3 EndZ=0
    g1: LineSegment StartX=5 StartY=3 StartZ=0 EndX=8 EndY=0 EndZ=0
    g2: LineSegment StartX=8 StartY=0 StartZ=0 EndX=8 EndY=-1.2 EndZ=0
    g3: LineSegment StartX=8 StartY=-1.2 StartZ=0 EndX=3.9 EndY=-1.2 EndZ=0
    g4: LineSegment StartX=3.9 StartY=-1.2 StartZ=0 EndX=3.9 EndY=-3 EndZ=0
    g5: LineSegment StartX=3.9 StartY=-3 StartZ=0 EndX=-3.9 EndY=-3 EndZ=0
    g6: LineSegment StartX=-3.9 StartY=-3 StartZ=0 EndX=-3.9 EndY=-1.2 EndZ=0
    g7: LineSegment StartX=-3.9 StartY=-1.2 StartZ=0 EndX=-8 EndY=-1.2 EndZ=0
    g8: LineSegment StartX=-8 StartY=-1.2 StartZ=0 EndX=-8 EndY=0 EndZ=0
    g9: LineSegment StartX=-8 StartY=0 StartZ=0 EndX=-5 EndY=3 EndZ=0
  constraints (28):
    c: PointOnObject(g1,g-1)
    c: Vertical(g2)
    c: Coincident(g3,g2)
    c: Horizontal(g3)
    c: Coincident(g4,g3)
    c: Coincident(g6,g5)
    c: Coincident(g7,g6)
    c: Horizontal(g7)
    c: Coincident(g8,g7)
    c: PointOnObject(g8,g-1)
    c: Vertical(g8)
    c: Coincident(g9,g0)
    c: Coincident(g0,g1)
    c: Coincident(g1,g2)
    c: Coincident(g5,g4)
    c: Vertical(g4)
    c: Vertical(g6)
    c: DistanceX(g0,g0) = 10
    c: Angle(g-1,g9) = 0.785398
    c: Coincident(g9,g8)
    c: Angle(g1,g-1) = 0.785398
    c: Symmetric(g0,g0,g-2)
    c: DistanceX(g5,g5) = 7.8
    c: Symmetric(g5,g4,g-2)
    c: DistanceY(g4,g4) = 1.8
    c: DistanceX(g7,g2) = 16
    c: DistanceY(g6,g6) = 1.8
    c: DistanceY(g5,g0) = 6
FEATURE [PartDesign::Pad] Pad001
  AddSubType = 0
  AlongSketchNormal = false
  CheckUpToFaceLimits = true
  ClaimChildren = false
  Direction = (0,0,1)
  Fit = 0
  FitJoin = 0
  InnerFit = 0
  InnerFitJoin = 0
  InnerTaperAngle = 0
  InnerTaperAngleRev = 0
  Length = 16
  Length2 = 100
  Linearize = true
  NewSolid = false
  Profile = -> Sketch002
  Suppress = false
  TreeRank = 12
  Type = 0
  _ProfileBasedVersion = 1
FEATURE [Sketcher::SketchObject] Sketch003
  FullyConstrained = true
  MapMode = 5
  Placement = pos=(0,-3,0) rot=(1,0,0;1.5708rad)
  Support = -> [Pad001]
  TreeRank = 13
  sketch-geometry (1):
    g0: Circle CenterX=0 CenterY=8 CenterZ=0 NormalX=0 NormalY=0 NormalZ=1 AngleXU=0 Radius=1.6
  constraints (3):
    c: PointOnObject(g0,g-2)
    c: DistanceY(g-1,g0) = 8
    c: Diameter(g0) = 3.2
FEATURE [PartDesign::Hole] Hole001
  AddSubType = 1
  BaseFeature = -> Pad001
  ClaimChildren = false
  CustomThreadClearance = 0
  Depth = 6
  DepthType = 0
  Diameter = 4.224
  DrillForDepth = false
  DrillPoint = 1
  DrillPointAngle = 118
  Fit = 0
  FitJoin = 0
  HoleCutCountersinkAngle = 90
  HoleCutCustomValues = false
  HoleCutDepth = 0
  HoleCutDiameter = 6.1
  HoleCutType = 0
  InnerFit = 0
  InnerFitJoin = 0
  Linearize = true
  ModelThread = true
  NewSolid = false
  Profile = -> Sketch003
  Suppress = false
  Tapered = false
  TaperedAngle = 90
  ThreadClass = 0
  ThreadDepth = 6
  ThreadDepthType = 1
  ThreadDirection = 0
  ThreadFit = 0
  ThreadSize = 13
  ThreadType = 1
  Threaded = true
  TreeRank = 14
  UseCustomThreadClearance = false
  _ProfileBasedVersion = 1
FEATURE [PartDesign::Body] Body001  label="M5T_nut"
  AutoGroupSolids = false
  ClaimAllChildren = false
  ExportMode = 0
  Group = -> [Sketch002,Pad001,Sketch003,Hole001]
  Origin = -> Origin001
  Tip = -> Hole001
  TreeRank = 780
  _ExportChildren = -> [Pad001,Hole001]
  _GroupVersion = 1
FEATURE [Sketcher::SketchObject] Sketch006
  FullyConstrained = true
  MapMode = 2
  Support = -> [XY_Plane003]
  TreeRank = 11
  expr: Constraints[20] = <<ТаблицаПараметров>>#<<Ролик>>.din6334_D1
  sketch-geometry (8):
    g0: LineSegment StartX=3.75278 StartY=6.5 StartZ=0 EndX=-3.75278 EndY=6.5 EndZ=0
    g1: LineSegment StartX=-3.75278 StartY=6.5 StartZ=0 EndX=-7.50555 EndY=2.04e-14 EndZ=0
    g2: LineSegment StartX=-7.50555 StartY=2.04e-14 StartZ=0 EndX=-3.75278 EndY=-6.5 EndZ=0
    g3: LineSegment StartX=-3.75278 StartY=-6.5 StartZ=0 EndX=3.75278 EndY=-6.5 EndZ=0
    g4: LineSegment StartX=3.75278 StartY=-6.5 StartZ=0 EndX=7.50555 EndY=1.78e-14 EndZ=0
    g5: LineSegment StartX=7.50555 StartY=1.8e-14 StartZ=0 EndX=3.75278 EndY=6.5 EndZ=0
    g6: Circle [constr] CenterX=0 CenterY=0 CenterZ=0 NormalX=0 NormalY=0 NormalZ=1 AngleXU=0 Radius=7.50555
    g7: Circle CenterX=0 CenterY=0 CenterZ=0 NormalX=0 NormalY=0 NormalZ=1 AngleXU=0 Radius=0.5
  constraints (18):
    c: Coincident(g0,g1)
    c: Coincident(g1,g2)
    c: Coincident(g2,g3)
    c: Coincident(g3,g4)
    c: Coincident(g4,g5)
    c: Coincident(g5,g0)
    c: Equal(g0, g1-g5) x5
    c: PointOnObject(g0,g6)
    c: PointOnObject(g1,g6)
    c: PointOnObject(g2,g6)
    c: PointOnObject(g3,g6)
    c: PointOnObject(g4,g6)
    c: PointOnObject(g5,g6)
    c: Horizontal(g0)
    c: Coincident(g6,g7)
    c: Coincident(g6,g-1)
    c: DistanceY(g2,g0) = 13
    c: Diameter(g7) = 1
FEATURE [PartDesign::Pad] Pad003
  AddSubType = 0
  AlongSketchNormal = false
  CheckUpToFaceLimits = true
  ClaimChildren = false
  Direction = (0,0,1)
  Fit = 0
  FitJoin = 0
  InnerFit = 0
  InnerFitJoin = 0
  InnerTaperAngle = 0
  InnerTaperAngleRev = 0
  Length = 24
  Length2 = 100
  Linearize = true
  NewSolid = false
  Profile = -> Sketch006
  Suppress = false
  TreeRank = 12
  Type = 0
  _ProfileBasedVersion = 1
  expr: Length = <<ТаблицаПараметров>>#<<Ролик>>.din6334_Len
FEATURE [PartDesign::Hole] Hole003
  AddSubType = 1
  BaseFeature = -> Pad003
  ClaimChildren = false
  CustomThreadClearance = 0
  Depth = 25
  DepthType = 0
  Diameter = 6.828
  DrillForDepth = false
  DrillPoint = 1
  DrillPointAngle = 118
  Fit = 0
  FitJoin = 0
  HoleCutCountersinkAngle = 90
  HoleCutCustomValues = false
  HoleCutDepth = 0
  HoleCutDiameter = 6.93
  HoleCutType = 0
  InnerFit = 0
  InnerFitJoin = 0
  Linearize = true
  ModelThread = true
  NewSolid = false
  Profile = -> Pad003 [Edge21]
  Suppress = false
  Tapered = false
  TaperedAngle = 90
  ThreadClass = 0
  ThreadDepth = 25
  ThreadDepthType = 0
  ThreadDirection = 0
  ThreadFit = 0
  ThreadSize = 16
  ThreadType = 1
  Threaded = true
  TreeRank = 13
  UseCustomThreadClearance = false
  _ProfileBasedVersion = 1
  expr: ThreadSize = <<ТаблицаПараметров>>#<<Ролик>>.din6334_Index
FEATURE [PartDesign::Body] Body003  label="DIN6334"
  AutoGroupSolids = false
  ClaimAllChildren = false
  ExportMode = 0
  Group = -> [Sketch006,Pad003,Hole003]
  Origin = -> Origin003
  Tip = -> Hole003
  TreeRank = 781
  _ExportChildren = -> [Pad003,Hole003]
  _GroupVersion = 1
FEATURE [Part::FeaturePython] Screw  label="M4x16-Screw"  # Fasteners workbench fastener (typed FeaturePython)
  TreeRank = 782
  diameter = 5
  invert = false
  length = 5
  lengthCustom = 16
  matchOuter = false
  offset = 0
  thread = false
  type = 34
FEATURE [Part::FeaturePython] Screw003  label="M5x12-Screw"  # Fasteners workbench fastener (typed FeaturePython)
  TreeRank = 783
  diameter = 6
  invert = false
  length = 2
  lengthCustom = 12
  matchOuter = false
  offset = 0
  thread = false
  type = 34
FEATURE [App::FeaturePython] Constraints  # WARN: FeaturePython — macro-defined, semantics opaque (R4)
  TreeRank = 785
  _LinkVersion = 1
  _Version = 1
FEATURE [Part::FeaturePython] Parts  # WARN: FeaturePython — macro-defined, semantics opaque (R4)
  Group = -> [Screw003]
  GroupMode = 0
  TreeRank = 787
  _LinkVersion = 1
FEATURE [App::FeaturePython] Constraints006  # WARN: FeaturePython — macro-defined, semantics opaque (R4)
  TreeRank = 791
  _LinkVersion = 1
  _Version = 1
FEATURE [Part::FeaturePython] Parts006  # WARN: FeaturePython — macro-defined, semantics opaque (R4)
  Group = -> [Screw]
  GroupMode = 0
  TreeRank = 793
  _LinkVersion = 1
FEATURE [Part::FeaturePython] Assembly005  label="КрепежМ6Тгайка"  # WARN: FeaturePython — macro-defined, semantics opaque (R4)
  AutoRelax = true
  BuildShape = 0
  Freeze = false
  Group = -> [Constraints005,Elements005,Parts005]
  TreeRank = 778
  Verbose = false
  _LinkVersion = 1
  _SolverType = 1
  _Version = 1
FEATURE [App::FeaturePython] Constraint065  label="Attachment029"  # WARN: FeaturePython — macro-defined, semantics opaque (R4)
  Cascade = false
  Disabled = false
  Group = -> [ElementLink138,ElementLink139]
  Multiply = false
  TreeRank = 773
  _ConstraintType = 45
  _LinkVersion = 1
  _Parent = -> Constraints005
FEATURE [App::FeaturePython] Constraints005  # WARN: FeaturePython — macro-defined, semantics opaque (R4)
  Group = -> [Constraint065]
  TreeRank = 762
  _LinkVersion = 1
  _Version = 1
FEATURE [Part::FeaturePython] Element140  label="Винт"  # link proxy (typed FeaturePython)
  Detach = false
  LinkTransform = true
  LinkedObject = -> Screw002 [Face5]
  TreeRank = 765
  _LinkVersion = 1
  _Parent = -> Elements005
FEATURE [Part::FeaturePython] Element141  label="резьбагайки"  # link proxy (typed FeaturePython)
  Detach = false
  LinkTransform = true
  LinkedObject = -> Link028 [Hole002.Face6]
  TreeRank = 766
  _LinkVersion = 1
  _Parent = -> Elements005
FEATURE [Part::FeaturePython] Element142  label="резьбавинта"  # link proxy (typed FeaturePython)
  Detach = false
  LinkTransform = true
  LinkedObject = -> Screw002 [Face7]
  TreeRank = 767
  _LinkVersion = 1
  _Parent = -> Elements005
FEATURE [App::FeaturePython] ElementLink138  label="резьбавинта"  # link proxy (typed FeaturePython)
  LinkTransform = true
  LinkedObject = -> Element142
  TreeRank = 774
  _LinkVersion = 1
  _Parent = -> Constraint065
FEATURE [App::FeaturePython] ElementLink139  label="резьбагайки"  # link proxy (typed FeaturePython)
  LinkTransform = true
  LinkedObject = -> Element141
  Offset = pos=(0,0,13) rot=(0,0,1;1.5708rad)
  Placement = pos=(-4.4e-15,1.13e-14,-13) rot=(0,0,-1;1.5708rad)
  TreeRank = 775
  _LinkVersion = 1
  _Parent = -> Constraint065
FEATURE [App::FeaturePython] Elements005  # WARN: FeaturePython — macro-defined, semantics opaque (R4)
  Group = -> [Element140,Element141,Element142]
  TreeRank = 763
  _LinkVersion = 1
FEATURE [Part::FeaturePython] Assembly  label="М5х12"  # WARN: FeaturePython — macro-defined, semantics opaque (R4)
  AutoRelax = true
  BuildShape = 0
  Freeze = false
  Group = -> [Constraints,Elements,Parts]
  TreeRank = 784
  Verbose = false
  _LinkVersion = 1
  _SolverType = 1
  _Version = 1
FEATURE [App::FeaturePython] Elements  # WARN: FeaturePython — macro-defined, semantics opaque (R4)
  Group = -> [Element]
  TreeRank = 786
  _LinkVersion = 1
FEATURE [Part::FeaturePython] Element  label="М5_12_посадка"  # link proxy (typed FeaturePython)
  Detach = false
  LinkTransform = true
  LinkedObject = -> Screw003 [Face5]
  TreeRank = 788
  _LinkVersion = 1
  _Parent = -> Elements
FEATURE [Part::FeaturePython] Assembly006  label="М4х16"  # WARN: FeaturePython — macro-defined, semantics opaque (R4)
  AutoRelax = true
  BuildShape = 0
  Freeze = false
  Group = -> [Constraints006,Elements006,Parts006]
  TreeRank = 790
  Verbose = false
  _LinkVersion = 1
  _SolverType = 1
  _Version = 1
FEATURE [App::FeaturePython] Elements006  # WARN: FeaturePython — macro-defined, semantics opaque (R4)
  Group = -> [Element143]
  TreeRank = 792
  _LinkVersion = 1
FEATURE [Part::FeaturePython] Element143  label="М4_16_посадка"  # link proxy (typed FeaturePython)
  Detach = false
  LinkTransform = true
  LinkedObject = -> Screw [Face5]
  TreeRank = 794
  _LinkVersion = 1
  _Parent = -> Elements006
---- part РоликY.FCStd = doc fcstd_d3a47af9ccbd ----
FCSTD DOCUMENT  (FreeCAD 0.21R38887 (Git))
Label: РоликY
License: All rights reserved
LicenseURL: http://en.wikipedia.org/wiki/All_rights_reserved
objects: App::FeaturePython×31, Part::FeaturePython×22, App::Link×7
note: 21 computed .brp shape members not serialized (recipe doc carries the construction recipe); baked Part::Feature solids carry a one-line shape summary decoded from their .brp
EXTERNAL_REF file=ТаблицаПараметров.FCStd obj=Spreadsheet002
EXTERNAL_REF file=роликЗащитыY.FCStd obj=Body
EXTERNAL_REF file=подшипник.FCStd obj=Body
EXTERNAL_REF file=Крепеж.FCStd obj=Body003
EXTERNAL_REF file=ТаблицаПараметров.FCStd obj=Spreadsheet004

FEATURE [Part::FeaturePython] Washer  label="M5-Washer"  # Fasteners workbench fastener (typed FeaturePython)
  InvalidShape = false
  Placement = pos=(110.2,-4e-16,2.59e-14) rot=(-0.707107,0,-0.707107;3.14159rad)
  TreeRank = 2
  ValidateShape = false
  diameter = 6
  invert = false
  matchOuter = false
  offset = 0
  type = 3
  expr: diameter = <<ТаблицаПараметров>>#<<Ролик>>.ShaibaIndex
FEATURE [App::Link] Link003  label="ШайбаПрав"
  AutoLinkLabel = true
  AutoPlacement = true
  LinkPlacement = pos=(-109.5,1e-15,2.55e-14) rot=(0,-1,0;4.71239rad)
  LinkedObject = -> Washer
  Placement = pos=(-109.5,1e-15,2.55e-14) rot=(0,-1,0;4.71239rad)
  SyncGroupVisibility = false
  TreeRank = 4
  _LinkVersion = 1
FEATURE [App::Link] Link006  label="РоликТело"
  AutoLinkLabel = false
  AutoPlacement = true
  LinkPlacement = pos=(1,-4e-16,2.51e-14) rot=(0,0,1;0rad)
  LinkedObject = -> <external роликЗащитыY.FCStd>#Body
  Placement = pos=(1,-4e-16,2.51e-14) rot=(0,0,1;0rad)
  SyncGroupVisibility = false
  TreeRank = 35
  _LinkOwner = 3305
  _LinkVersion = 1
FEATURE [App::Link] Link  label="Подшипник"
  AutoLinkLabel = false
  AutoPlacement = true
  LinkPlacement = pos=(108.7,-4e-16,2.54e-14) rot=(1,0,0;4.71239rad)
  LinkedObject = -> <external подшипник.FCStd>#Body
  Placement = pos=(108.7,-4e-16,2.54e-14) rot=(1,0,0;4.71239rad)
  SyncGroupVisibility = false
  TreeRank = 57
  _LinkOwner = 3305
  _LinkVersion = 1
FEATURE [App::Link] Link007  label="Подшипник2"
  AutoLinkLabel = true
  AutoPlacement = true
  LinkPlacement = pos=(-106.9,2e-16,2.54e-14) rot=(-1,0,0;4.71239rad)
  LinkedObject = -> Link
  Placement = pos=(-106.9,2e-16,2.54e-14) rot=(-1,0,0;4.71239rad)
  SyncGroupVisibility = false
  TreeRank = 58
  _LinkVersion = 1
FEATURE [App::Link] Link008  label="DIN6334_1"
  AutoLinkLabel = true
  AutoPlacement = true
  LinkPlacement = pos=(105.2,0,2.49e-14) rot=(-0.707107,0,0.707107;3.14159rad)
  LinkedObject = -> <external Крепеж.FCStd>#Body003
  Placement = pos=(105.2,0,2.49e-14) rot=(-0.707107,0,0.707107;3.14159rad)
  SyncGroupVisibility = false
  TreeRank = 86
  _LinkVersion = 1
FEATURE [App::Link] Link009  label="DIN6334_2"
  AutoLinkLabel = true
  AutoPlacement = true
  LinkPlacement = pos=(-103.4,-9e-16,2.51e-14) rot=(0,1,0;1.5708rad)
  LinkedObject = -> Link008
  Placement = pos=(-103.4,-9e-16,2.51e-14) rot=(0,1,0;1.5708rad)
  SyncGroupVisibility = false
  TreeRank = 1
  _LinkVersion = 1
FEATURE [Part::FeaturePython] ThreadedRod  label="M5x195.0-ThreadedRod"  # Fasteners workbench fastener (typed FeaturePython)
  InvalidShape = false
  Placement = pos=(-97.3,0,2.71407e-11) rot=(0.707107,0,-0.707107;3.14159rad)
  TreeRank = 97
  ValidateShape = false
  diameter = 7
  diameterCustom = 6
  invert = false
  leftHanded = false
  length = 195
  matchOuter = false
  offset = 0
  pitchCustom = 1
  thread = false
  type = 4
  expr: diameter = <<ТаблицаПараметров>>#<<Ролик>>.ShpilkaIndex
  expr: length = <<ТаблицаПараметров>>#<<Ролик>>.dimL1 - <<ТаблицаПараметров>>#<<Ролик>>.dimH3 * 2 - <<ТаблицаПараметров>>#<<Ролик>>.din6334_Len
FEATURE [Part::FeaturePython] Screw  label="M5x12-Screw"  # Fasteners workbench fastener (typed FeaturePython)
  InvalidShape = false
  Placement = pos=(113.8,-1e-16,1.126e-13) rot=(0,1,0;1.5708rad)
  TreeRank = 106
  ValidateShape = false
  diameter = 3
  invert = false
  leftHanded = false
  length = 2
  lengthCustom = 12
  matchOuter = false
  offset = 0
  thread = false
  type = 40
  expr: diameter = <<ТаблицаПараметров>>#<<Ролик>>.IndexVinta
  expr: length = <<ТаблицаПараметров>>#<<Ролик>>.dlinaVintaInd
FEATURE [App::Link] Link010  label="ВинтПрав"
  AutoLinkLabel = true
  AutoPlacement = true
  LinkPlacement = pos=(-112,1.1e-15,-1.03e-13) rot=(0.707107,0,-0.707107;3.14159rad)
  LinkedObject = -> Screw
  Placement = pos=(-112,1.1e-15,-1.03e-13) rot=(0.707107,0,-0.707107;3.14159rad)
  SyncGroupVisibility = false
  TreeRank = 107
  _LinkVersion = 1
FEATURE [Part::FeaturePython] Parts  # WARN: FeaturePython — macro-defined, semantics opaque (R4)
  Group = -> [Link006,Link,Link007,Link003,Washer,ThreadedRod,Link008,Link009,Screw,Link010]
  GroupMode = 0
  InvalidShape = false
  TreeRank = 0
  ValidateShape = false
  _LinkVersion = 1
FEATURE [Part::FeaturePython] Assembly  label="Ролик"  # WARN: FeaturePython — macro-defined, semantics opaque (R4)
  AutoRelax = true
  BuildShape = 0
  Configuration = 0
  Freeze = false
  Group = -> [Constraints,Elements,Parts]
  InvalidShape = false
  Placement = pos=(0,0,50) rot=(0,0,1;0rad)
  TreeRank = 0
  ValidateShape = false
  Verbose = false
  _LinkVersion = 1
  _SolverType = 1
  _Version = 1
  expr: Configuration.Enum = ТаблицаПараметров#Spreadsheet002.cells[<<B14:|>>]
FEATURE [App::FeaturePython] Constraints  # WARN: FeaturePython — macro-defined, semantics opaque (R4)
  Group = -> [Constraint,Constraint005,Constraint006,Constraint009,Constraint010,Constraint011,Constraint013,Constraint014,Constraint015,Constraint016]
  TreeRank = 0
  _LinkVersion = 1
  _Version = 1
FEATURE [App::FeaturePython] Elements  # WARN: FeaturePython — macro-defined, semantics opaque (R4)
  Group = -> [Element,Element001,Element006,Element007,Element008,Element009,Element010,Element011,Element012,Element013,Element014,Element015,Element016,Element017,Element018,Element019,Element020]
  TreeRank = 0
  _LinkVersion = 1
FEATURE [Part::FeaturePython] Element  label="ТелоПосадкаЛв"  # link proxy (typed FeaturePython)
  Detach = false
  InvalidShape = false
  LinkTransform = true
  LinkedObject = -> Link006 [Revolution.Face5]
  TreeRank = 108
  ValidateShape = false
  _LinkVersion = 1
  _Parent = -> Elements
FEATURE [Part::FeaturePython] Element001  label="ТелоПосадкаПр"  # link proxy (typed FeaturePython)
  Detach = false
  InvalidShape = false
  LinkTransform = true
  LinkedObject = -> Link006 [Revolution.Face7]
  TreeRank = 109
  ValidateShape = false
  _LinkVersion = 1
  _Parent = -> Elements
FEATURE [Part::FeaturePython] Element006  label="ЛвШайбНиз"  # link proxy (typed FeaturePython)
  Detach = false
  InvalidShape = false
  LinkTransform = true
  LinkedObject = -> Washer [Face3]
  TreeRank = 114
  ValidateShape = false
  _LinkVersion = 1
  _Parent = -> Elements
FEATURE [Part::FeaturePython] Element007  label="ПрШайбНиз"  # link proxy (typed FeaturePython)
  Detach = false
  InvalidShape = false
  LinkTransform = true
  LinkedObject = -> Link003 [Face1]
  TreeRank = 115
  ValidateShape = false
  _LinkVersion = 1
  _Parent = -> Elements
FEATURE [Part::FeaturePython] Element008  label="ЛвШайбВерх"  # link proxy (typed FeaturePython)
  Detach = false
  InvalidShape = false
  LinkTransform = true
  LinkedObject = -> Washer [Face1]
  TreeRank = 116
  ValidateShape = false
  _LinkVersion = 1
  _Parent = -> Elements
FEATURE [Part::FeaturePython] Element009  label="ПрШайбВерх"  # link proxy (typed FeaturePython)
  Detach = false
  InvalidShape = false
  LinkTransform = true
  LinkedObject = -> Link003 [Face3]
  TreeRank = 117
  ValidateShape = false
  _LinkVersion = 1
  _Parent = -> Elements
FEATURE [Part::FeaturePython] Element010  label="ЛвГайкаНиз"  # link proxy (typed FeaturePython)
  Detach = false
  InvalidShape = false
  LinkTransform = true
  LinkedObject = -> Link008 [Hole003.Face5]
  TreeRank = 118
  ValidateShape = false
  _LinkVersion = 1
  _Parent = -> Elements
FEATURE [Part::FeaturePython] Element011  label="ПрГайкаНиз"  # link proxy (typed FeaturePython)
  Detach = false
  InvalidShape = false
  LinkTransform = true
  LinkedObject = -> Link009 [Hole003.Face5]
  TreeRank = 119
  ValidateShape = false
  _LinkVersion = 1
  _Parent = -> Elements
FEATURE [Part::FeaturePython] Element012  label="ЛвГайкаВерх"  # link proxy (typed FeaturePython)
  Detach = false
  InvalidShape = false
  LinkTransform = true
  LinkedObject = -> Link008 [Hole003.Face4]
  TreeRank = 120
  ValidateShape = false
  _LinkVersion = 1
  _Parent = -> Elements
FEATURE [Part::FeaturePython] Element013  label="ПрГайкаВерх"  # link proxy (typed FeaturePython)
  Detach = false
  InvalidShape = false
  LinkTransform = true
  LinkedObject = -> Link009 [Hole003.Face4]
  TreeRank = 121
  ValidateShape = false
  _LinkVersion = 1
  _Parent = -> Elements
FEATURE [Part::FeaturePython] Element014  label="ВинтЛв"  # link proxy (typed FeaturePython)
  Detach = false
  InvalidShape = false
  LinkTransform = true
  LinkedObject = -> Screw [Edge4]
  TreeRank = 122
  ValidateShape = false
  _LinkVersion = 1
  _Parent = -> Elements
FEATURE [Part::FeaturePython] Element015  label="ВинтПр"  # link proxy (typed FeaturePython)
  Detach = false
  InvalidShape = false
  LinkTransform = true
  LinkedObject = -> Link010 [Edge4]
  TreeRank = 123
  ValidateShape = false
  _LinkVersion = 1
  _Parent = -> Elements
FEATURE [Part::FeaturePython] Element016  label="ШпилькаСлева"  # link proxy (typed FeaturePython)
  Detach = false
  InvalidShape = false
  LinkTransform = true
  LinkedObject = -> ThreadedRod [Edge6]
  TreeRank = 124
  ValidateShape = false
  _LinkVersion = 1
  _Parent = -> Elements
FEATURE [App::FeaturePython] Constraint  label="Locked"  # WARN: FeaturePython — macro-defined, semantics opaque (R4)
  Disabled = false
  Group = -> [ElementLink]
  TreeRank = 125
  _ConstraintType = 0
  _LinkVersion = 1
  _Parent = -> Constraints
FEATURE [App::FeaturePython] ElementLink  label="ТелоПосадкаЛв"  # link proxy (typed FeaturePython)
  LinkTransform = true
  LinkedObject = -> Element
  TreeRank = 126
  _LinkVersion = 1
  _Parent = -> Constraint
FEATURE [App::FeaturePython] Constraint005  label="Attachment004"  # WARN: FeaturePython — macro-defined, semantics opaque (R4)
  Cascade = false
  Disabled = false
  Group = -> [ElementLink009,ElementLink010]
  Multiply = false
  TreeRank = 139
  _ConstraintType = 45
  _LinkVersion = 1
  _Parent = -> Constraints
FEATURE [App::FeaturePython] ElementLink009  label="ВинтЛв"  # link proxy (typed FeaturePython)
  LinkTransform = true
  LinkedObject = -> Element014
  Offset = pos=(0,0,-1.5) rot=(1,0,0;3.14159rad)
  Placement = pos=(226.1,1.36e-14,-1.004e-13) rot=(0,0,1;3.14159rad)
  TreeRank = 140
  _LinkVersion = 1
  _Parent = -> Constraint005
  expr: Offset.Base.z = -<<ТаблицаПараметров>>#<<ЗащитаТабл>>.toldhinZashita
FEATURE [App::FeaturePython] ElementLink010  label="ЛвШайбВерх"  # link proxy (typed FeaturePython)
  LinkTransform = true
  LinkedObject = -> Element008
  TreeRank = 141
  _LinkVersion = 1
  _Parent = -> Constraint005
FEATURE [App::FeaturePython] Constraint006  label="Attachment005"  # WARN: FeaturePython — macro-defined, semantics opaque (R4)
  Cascade = false
  Disabled = false
  Group = -> [ElementLink011,ElementLink012]
  Multiply = false
  TreeRank = 142
  _ConstraintType = 45
  _LinkVersion = 1
  _Parent = -> Constraints
FEATURE [App::FeaturePython] ElementLink011  label="ВинтПр"  # link proxy (typed FeaturePython)
  LinkTransform = true
  LinkedObject = -> Element015
  Offset = pos=(0,0,-1.5) rot=(1,0,0;3.14159rad)
  Placement = pos=(-222.5,-1.17e-14,-8.8435e-12) rot=(0,0,1;3.14159rad)
  TreeRank = 143
  _LinkVersion = 1
  _Parent = -> Constraint006
  expr: Offset.Base.z = -<<ТаблицаПараметров>>#<<ЗащитаТабл>>.toldhinZashita
FEATURE [App::FeaturePython] ElementLink012  label="ПрШайбВерх"  # link proxy (typed FeaturePython)
  LinkTransform = true
  LinkedObject = -> Element009
  TreeRank = 144
  _LinkVersion = 1
  _Parent = -> Constraint006
FEATURE [App::FeaturePython] Constraint009  label="Attachment008"  # WARN: FeaturePython — macro-defined, semantics opaque (R4)
  Cascade = false
  Disabled = false
  Group = -> [ElementLink018,ElementLink019]
  Multiply = false
  TreeRank = 151
  _ConstraintType = 45
  _LinkVersion = 1
  _Parent = -> Constraints
FEATURE [App::FeaturePython] ElementLink018  label="ЛвГайкаНиз"  # link proxy (typed FeaturePython)
  LinkTransform = true
  LinkedObject = -> Element010
  TreeRank = 153
  _LinkVersion = 1
  _Parent = -> Constraint009
FEATURE [App::FeaturePython] ElementLink019  label="ШпилькаСлева"  # link proxy (typed FeaturePython)
  LinkTransform = true
  LinkedObject = -> Element016
  Offset = pos=(0,0,7.5) rot=(0,0,1;0rad)
  Placement = pos=(-7.5,-4e-16,-2.0692e-12) rot=(0,0,1;0rad)
  TreeRank = 155
  _LinkVersion = 1
  _Parent = -> Constraint009
  expr: Offset.Base.z = <<ТаблицаПараметров>>#<<Ролик>>.din6334_Len / 2
FEATURE [Part::FeaturePython] Element017  label="ЛвПодшНиз"  # link proxy (typed FeaturePython)
  Detach = false
  InvalidShape = false
  LinkTransform = true
  LinkedObject = -> Link [Revolution.Face2]
  TreeRank = 156
  ValidateShape = false
  _LinkVersion = 1
  _Parent = -> Elements
FEATURE [Part::FeaturePython] Element018  label="ПрПодшВерх"  # link proxy (typed FeaturePython)
  Detach = false
  InvalidShape = false
  LinkTransform = true
  LinkedObject = -> Link007 [Revolution.Face2]
  TreeRank = 157
  ValidateShape = false
  _LinkVersion = 1
  _Parent = -> Elements
FEATURE [Part::FeaturePython] Element019  label="ПрПодшНиз"  # link proxy (typed FeaturePython)
  Detach = false
  InvalidShape = false
  LinkTransform = true
  LinkedObject = -> Link007 [Revolution.Face4]
  TreeRank = 158
  ValidateShape = false
  _LinkVersion = 1
  _Parent = -> Elements
FEATURE [Part::FeaturePython] Element020  label="ЛвПодшВерх"  # link proxy (typed FeaturePython)
  Detach = false
  InvalidShape = false
  LinkTransform = true
  LinkedObject = -> Link [Revolution.Face4]
  TreeRank = 159
  ValidateShape = false
  _LinkVersion = 1
  _Parent = -> Elements
FEATURE [App::FeaturePython] Constraint010  label="ТелоЛв"  # WARN: FeaturePython — macro-defined, semantics opaque (R4)
  Cascade = false
  Disabled = false
  Group = -> [ElementLink020,ElementLink021]
  Multiply = false
  TreeRank = 160
  _ConstraintType = 45
  _LinkVersion = 1
  _Parent = -> Constraints
FEATURE [App::FeaturePython] ElementLink020  label="ТелоПосадкаЛв"  # link proxy (typed FeaturePython)
  LinkTransform = true
  LinkedObject = -> Element
  TreeRank = 161
  _LinkVersion = 1
  _Parent = -> Constraint010
FEATURE [App::FeaturePython] ElementLink021  label="ЛвПодшНиз"  # link proxy (typed FeaturePython)
  LinkTransform = true
  LinkedObject = -> Element017
  TreeRank = 162
  _LinkVersion = 1
  _Parent = -> Constraint010
FEATURE [App::FeaturePython] Constraint011  label="ТелоПр"  # WARN: FeaturePython — macro-defined, semantics opaque (R4)
  Cascade = false
  Disabled = false
  Group = -> [ElementLink022,ElementLink023]
  Multiply = false
  TreeRank = 163
  _ConstraintType = 45
  _LinkVersion = 1
  _Parent = -> Constraints
FEATURE [App::FeaturePython] ElementLink022  label="ТелоПосадкаПр"  # link proxy (typed FeaturePython)
  LinkTransform = true
  LinkedObject = -> Element001
  TreeRank = 164
  _LinkVersion = 1
  _Parent = -> Constraint011
FEATURE [App::FeaturePython] ElementLink023  label="ПрПодшНиз"  # link proxy (typed FeaturePython)
  LinkTransform = true
  LinkedObject = -> Element019
  Offset = pos=(0,0,0) rot=(1,0,0;3.14159rad)
  Placement = pos=(-208.8,-1.37e-14,-2.8e-15) rot=(0,0,1;3.14159rad)
  TreeRank = 165
  _LinkVersion = 1
  _Parent = -> Constraint011
FEATURE [App::FeaturePython] Constraint013  label="Attachment011"  # WARN: FeaturePython — macro-defined, semantics opaque (R4)
  Cascade = false
  Disabled = false
  Group = -> [ElementLink026,ElementLink027]
  Multiply = false
  TreeRank = 169
  _ConstraintType = 45
  _LinkVersion = 1
  _Parent = -> Constraints
FEATURE [App::FeaturePython] ElementLink026  label="ПрПодшВерх"  # link proxy (typed FeaturePython)
  LinkTransform = true
  LinkedObject = -> Element018
  TreeRank = 170
  _LinkVersion = 1
  _Parent = -> Constraint013
FEATURE [App::FeaturePython] ElementLink027  label="ПрШайбНиз"  # link proxy (typed FeaturePython)
  LinkTransform = true
  LinkedObject = -> Element007
  TreeRank = 171
  _LinkVersion = 1
  _Parent = -> Constraint013
FEATURE [App::FeaturePython] Constraint014  label="Attachment012"  # WARN: FeaturePython — macro-defined, semantics opaque (R4)
  Cascade = false
  Disabled = false
  Group = -> [ElementLink028,ElementLink029]
  Multiply = false
  TreeRank = 172
  _ConstraintType = 45
  _LinkVersion = 1
  _Parent = -> Constraints
FEATURE [App::FeaturePython] ElementLink028  label="ЛвГайкаВерх"  # link proxy (typed FeaturePython)
  LinkTransform = true
  LinkedObject = -> Element012
  TreeRank = 173
  _LinkVersion = 1
  _Parent = -> Constraint014
FEATURE [App::FeaturePython] ElementLink029  label="ЛвПодшНиз"  # link proxy (typed FeaturePython)
  LinkTransform = true
  LinkedObject = -> Element017
  TreeRank = 174
  _LinkVersion = 1
  _Parent = -> Constraint014
FEATURE [App::FeaturePython] Constraint015  label="Attachment013"  # WARN: FeaturePython — macro-defined, semantics opaque (R4)
  Cascade = false
  Disabled = false
  Group = -> [ElementLink030,ElementLink031]
  Multiply = false
  TreeRank = 175
  _ConstraintType = 45
  _LinkVersion = 1
  _Parent = -> Constraints
FEATURE [App::FeaturePython] ElementLink030  label="ПрГайкаВерх"  # link proxy (typed FeaturePython)
  LinkTransform = true
  LinkedObject = -> Element013
  Placement = pos=(0,1.64e-14,0) rot=(0,0,1;0rad)
  TreeRank = 176
  _LinkVersion = 1
  _Parent = -> Constraint015
FEATURE [App::FeaturePython] ElementLink031  label="ПрПодшНиз"  # link proxy (typed FeaturePython)
  LinkTransform = true
  LinkedObject = -> Element019
  Placement = pos=(0,1.64e-14,0) rot=(0,0,1;0rad)
  TreeRank = 177
  _LinkVersion = 1
  _Parent = -> Constraint015
FEATURE [App::FeaturePython] Constraint016  label="Attachment"  # WARN: FeaturePython — macro-defined, semantics opaque (R4)
  Cascade = false
  Disabled = false
  Group = -> [ElementLink032,ElementLink033]
  Multiply = false
  TreeRank = 178
  _ConstraintType = 45
  _LinkVersion = 1
  _Parent = -> Constraints
FEATURE [App::FeaturePython] ElementLink032  label="ЛвПодшВерх"  # link proxy (typed FeaturePython)
  LinkTransform = true
  LinkedObject = -> Element020
  TreeRank = 179
  _LinkVersion = 1
  _Parent = -> Constraint016
FEATURE [App::FeaturePython] ElementLink033  label="ЛвШайбНиз"  # link proxy (typed FeaturePython)
  LinkTransform = true
  LinkedObject = -> Element006
  TreeRank = 180
  _LinkVersion = 1
  _Parent = -> Constraint016
---- part ТаблицаПараметров.FCStd = doc fcstd_60ae2dd5e8f4 ----
FCSTD DOCUMENT  (FreeCAD 0.21R38887 (Git))
Label: ТаблицаПараметров
License: All rights reserved
LicenseURL: http://en.wikipedia.org/wiki/All_rights_reserved
objects: Spreadsheet::Sheet×9
EXTERNAL_REF file=ЧастиСтанка/Станина/Деталі/NEMA23.FCStd obj=Assembly

FEATURE [Spreadsheet::Sheet] Spreadsheet  label="Профиль"
  PythonMode = false
  ShowCells = 0
  TreeRank = 1
  cells = A2=ДлинаПрофиля; B2(Dlina)==<<ТаблСтанина>>.ShirinaStaninu; A3=ШагОтверстийСоединения; B3(ShagOtv)=100; A4=ДиаметрОтверстия; B4(DiametrOtvSoed)=4; A6=Перша висота Т пазу; B6(HTpaz1)=20; A7=Друга висота Т пазу; B7(HTpaz2)=60; A8=КоличествоОтвСоединения; B8(HoleNumberSoed)==trunc(Dlina / ShagOtv) - 1; A9=ДлинаМасиваСоед; B9(DlinaMasivaSoed)==ShagOtv * HoleNumberSoed; A10=ОтступОтКрая; B10(OtstupRels)==(Dlina - DlinaMasivaSoed) / 2
FEATURE [Spreadsheet::Sheet] Spreadsheet001  label="ТаблСтанина"
  PythonMode = false
  ShowCells = 0
  TreeRank = 0
  cells = A2=Ширина; B2(ShirinaStaninu)=480; A3=Количество палок профиля; B3(NumberProfileBody)=10; A4=Высота; B4(RazmerProfilja)=80; A5=Глубина; B5(GlubinaStaninu)==RazmerProfilja * NumberProfileBody
FEATURE [Spreadsheet::Sheet] Spreadsheet002  label="Ролик"
  PythonMode = false
  ShowCells = 0
  TreeRank = 1
  cells = A7=Высота под подшипник; B7(dimH3)==dimH1 + dimH2; C7=висота   подш + висота шайби; A8=Длина общая (без шайб); B8(dimL1)=222; C8=Final lenght; A9=ball radius; B9(ball_radius)==(<<Ролик>>.dimD2 / 2 - <<Ролик>>.diamPodsh / 2) / 3; C9=alpha; D9(alpa)==atan(.ball_radius / .ball_pos_radius); A10=R for ball; B10(ball_pos_radius)==(<<Ролик>>.dimD2 / 2 - <<Ролик>>.diamPodsh / 2) / 2 + <<Ролик>>.diamPodsh / 2; C10=number of ball; D10(ball_number)==trunc(360 / (2 * .alpa)); C11=Длинная гайка; G11=Винт; I11=Подшипник; L11=Труба; N11=Шайба; O11=Шпилька; B12=Inner thread; C12=External dim; D12=Thread index; E12=Lenght; F12=ШайбаИндекс; G12=Индекс винта; H12=Длина винта(index); I12=Диам подш; J12=диад внутр подш; K12=Высота подш.; L12=Диам внешн.; M12=Диам внутр.; N12=Высота шайбы; O12=Индекс; A13=DIN6334 table; B13==dbind(РоликY#Assembly.Configuration.All); C13(din6334_D1)==.C14; D13(din6334_Index)==.D14; E13(din6334_Len)==.E14; F13(ShaibaIndex)==.F14; G13(IndexVinta)==.G14; H13(dlinaVintaInd)==.H14; I13(dimD2)==.I14; J13(diamPodsh)==.J14; K13(dimH1)==.K14; L13(dimD1)==.L14; M13(dimD3)==.M14; N13(dimH2)==.N14; O13(ShpilkaIndex)==.O14; B14=M5v1; C14=8; D14=13; E14=15; F14=6; G14=3; H14=2; I14=14; J14=5; K14=5; L14=16; M14=12; N14=1; O14=7; B15=M5v2; C15=8; D15=13; E15=15; F15=6; G15=3; H15=2; I15=16; J15=5; K15=5; L15=18; M15=14; N15=1; O15=7; B16=M6; C16=10; D16=14; E16=18; F16=7; G16=4; H16=2; I16=19; J16=6; K16=6; L16=21.3; M16=16.1; N16=1.6; O16=8; B17=M8; C17=13; D17=16; E17=24; F17=8; G17=5; H17=3; I17=22; J17=8; K17=7; L17=25; M17=19; N17=1.6; O17=9
  expr: cells.Bind.C13.ZZ13 = tuple(.cells, <<C>> + str(hiddenref(РоликY#Assembly.Configuration) + 14), <<ZZ>> + str(hiddenref(РоликY#Assembly.Configuration) + 14))
FEATURE [Spreadsheet::Sheet] Spreadsheet004  label="ЗащитаТабл"
  PythonMode = false
  ShowCells = 0
  TreeRank = 1
  cells = A2=Ширина 1; B2(dimL1)=45; C2=Слева от П прорези (зависит от опоры и толщины пластины крепления опоры); D2=dimL1; E2=задать формулу; A3=Ширина 2; B3(dimL2)==<<ТаблСтанина>>.GlubinaStaninu; C3=П прорезь Зависит от ширины профиля и количества палок + небольшой зазор (0.2мм); D3=dimL2; A4=Ширина 3; B4(dimL3)==ceil((<<NEMA23Table>>.TotalLen + dimR1 * 2 + 5) / 5) * 5 + 10; C4=Справа от П прорези (motor); D4=dimL3; A5=Высота 1; B5(dimH1)==<<ПластиныY>>.Heigh1; C5=Общая высота защиты; D5=dimH1; E5=висота пластин и защити однакові; A6=Высота 2; B6(dimh2)=80; C6=Высота профиля ; D6=dimh2; A7=Радиус 1; B7(dimR1)==<<Ролик>>.dimD1 / 2; C7=Радиус скругления по углам с роликами; D7=dimR1; A8=Радиус 2; B8(dimR2)=2.5; C8=Крепление роликов; D8=dimR2; A9=Радиус 3; B9(dimR3)==<<ПроставкаYТабл>>.DiamOtvZashitu / 2; C9=Крепление защиты(радиус отверстя); D9=dimR3; A10=Радиус 4; B10(dimR4)=3; C10=Скругление в точках прилегания к профилю; D10=dimR4; A11=Высота 3; B11(dimH3)==<<ПроставкаYТабл>>.Tolshina / 2; C11=Высота винтов крепления защиты; D11=dimH3; A12=ЧислоВинтов1; B12(num1)==<<ПроставкаYТабл>>.NumberHoleZashita; C12=Количество винтов крепления защиты; D12=num1; A13=Шаг1; B13(dimL4)==<<ПроставкаYТабл>>.ShagOtvZash; C13=Расстояние между винтами защиты; D13=dimL4; A14=ДлинаМасива1; B14(dimL5)==num1 * dimL4; C14=Растояние между крайними віинтами защиты; D14=dimL5; A15=Отступ1; B15(dimL6)==(dimL2 - dimL5) / 2; C15=Отступ от начала П прорези до первого винта крепления защиты; D15=dimL6; A16=Толщина листа; B16(toldhinZashita)=1.5; D16=toldhinZashita
FEATURE [Spreadsheet::Sheet] Spreadsheet006  label="ШВП"
  PythonMode = false
  ShowCells = 0
  TreeRank = 2
  cells = A1=ШВП Х; A7=ШВП Y; B7=Длина общая; C7=Диаметр под гайку; D7=Длина резьбы под гайку; E7=Длина вала под крепление; F7=Длина вала под муфту; G7=Диаметр вала под муфту; H7=Шаг ШВП; I7=Диаметр ШВП; B8(lenY)=407; C8(diamYval)=12; D8(lenRezbaYval1)=10; E8(lenValY1)=36; F8(lenMuftaY)=10; G8(diamMuftaY)=10; H8(ShagScrewY)=5; I8(diamSrewY)=16; A12=ШВП Z
FEATURE [Spreadsheet::Sheet] Spreadsheet007  label="ПластиныY"
  PythonMode = false
  ShowCells = 0
  TreeRank = 3
  cells = A1=Параметры пластин для крепления мотора; A3=Ширина пластины; B3(Len1)=145; A4=Висота пластини; B4(Heigh1)=129; A5=ШВП висота ; B5(Heigh2)=100
FEATURE [Spreadsheet::Sheet] Spreadsheet005  label="ПроставкаYТабл"
  Body = -1
  Configuration = 3
  PythonMode = false
  ShowCells = 0
  TreeRank = 5
  cells = A1=Наименование; B1=Значение; C1=Описание параметра; D1=Наименование; E1=Значение; F1=Описание; A2=ДлинаОбщая; D2=Количество точек крепления защиты; E2(NumberHoleZashita)=7; A3=Толщина Проставки; B3(Tolshina)=25; D3=Шаг отверстий под защиту; E3(ShagOtvZash)==<<ТаблСтанина>>.GlubinaStaninu / (NumberHoleZashita + 1); A4=Ширина Проставки; B4(Shirina)=35; D4=ДлинаМасиваКрепежаЗащиты; E4(DlinaMasivaZashita)==NumberHoleZashita * ShagOtvZash; A5=Отступ от края(основание); B5(BodyFirstHole)=20; C5=Отступ от центра; D5(OtstupCenter)==<<ТаблСтанина>>.GlubinaStaninu / 2 - BodyFirstHole; A6=ШагОтверстий; B6(ShagOtverastij)=40; A8=КоличествоОтверстий; B8(HoleNumber)==trunc((<<ТаблСтанина>>.GlubinaStaninu - BodyFirstHole) / ShagOtverastij); A9=ДлинаЛинМасива; B9(DlinaMasiva)==ShagOtverastij * HoleNumber; A11=КоличествоОтвРельс; B11(HoleNumberRels)==trunc(<<ТаблСтанина>>.GlubinaStaninu / ShagRelsa) - 1; A12=ДлинаМасиваРельс; B12(DlinaMasivaRels)==ShagRelsa * HoleNumberRels; A13=ОтступОтКраяРельса; B13(OtstupRels)==(<<ТаблСтанина>>.GlubinaStaninu - DlinaMasivaRels) / 2; A15=КрепежПроставки; B15=ДиаметрОтверстияПодВинт; C15=ДиаметрОтверстия подГоловку; D15=ГлубинаОтверстияПодГоловку; B16(Body_holeDiam)==.B18; C16(BodyHoleDiam)==.C18; D16(BodyHoleGlubina)==.D18; A17=M3; B17=3.2; C17=6; D17=3.4; A18=M4; B18=4.3; C18=8; D18=4.6; A19=M5; B19=5.3; C19=10; D19=5.7; A20=M6; B20=6.4; C20=11; D20=6.8; B24=Ширина Рельсы; C24=Глубина Посадки; D24=Шаг отверстий; E24=Крепление рельсы (индекс резьбы); F24=Длина Винта Крепления; G24=ГлубинаОтверстияПодВИнт; B25(ShirinaPaza)==.B28; C25(GlubunaPaza)==.C28; D25(ShagRelsa)==.D28; E25(indexKreplRels)==.E28; F25(DlinaVintaRels)==.F28; G25(GlubinaOtvRels)==.G28; A26=HGH15; B26=15; C26=4.3; D26=60; E26=11; F26=16; G26=6; A27=HGH20; B27=20; C27=4.6; D27=60; E27=13; F27=16; G27=8; A28=HGH25; B28=23; C28=5.5; D28=60; E28=14; F28=20; G28=8; A32=Крепление боковой защиты; C32=Глубина отверстия под резьбу; D32=Диаметр отверстия в пластине защиты; B33(indexZashita)==.B38; C33(GlubinaOtvZashitu)==.C38; D33(DiamOtvZashitu)==.D38; A34=M3x10; B34=9; C34=10; D34=3.2; A35=M3x12; B35=9; C35=12; D35=3.2; A36=M4x10; B36=11; C36=10; D36=4.3; A37=M4x12; B37=11; C37=12; D37=4.3; A38=M5x10; B38=13; C38=10; D38=5.3; A39=M5x12; B39=13; C39=12; D39=5.3
  expr: Body.Enum = cells[<<A40:|>>]
  expr: Configuration.Enum = cells[<<A17:|>>]
FEATURE [Spreadsheet::Sheet] Spreadsheet009  label="NEMA23Table"
  PythonMode = false
  ShowCells = 0
  TreeRank = 6
  cells = A1=Тип Мотора; B1=Длина мотора; C1=Длина Тела мотора; D1=Длина Вала; E1=Відстань між отворами кріплення; F1=Діаметр кріплення мотора; G1=Діаметр посадки мотора; H1=Діаметр отвору для різьби; B3(TotalLen)==.B12; C3(BodyLen)==.C12; D3(DlinaVala)==.D12; E3(DistOtv)=47.14; F3(DiamOtv)=5; G3(PosadkaMotor)=38.1; H3(diamRezba)=4.2; A4=23HD2304; B4=45; C4=22; D4=63.4; A5=23HD3005; B5=54; C5=31; D5=72.4; A6=23HD4004; B6=56; C6=33; D6=74.4; A7=23HD5401; B7=65; C7=42; D7=83.4; A8=23HD6001; B8=76; C8=53; D8=94.4; A9=23HD8434; B9=100; C9=77; D9=118.4; A10=23HD2601; B10=45; C10=22; D10=63.4; A11=23HD6603; B11=76; C11=53; D11=94.4; A12=23HD7801; B12=82; C12=59; D12=100.4
  expr: cells.Bind.B3.D3 = tuple(.cells, <<B>> + str(hiddenref(NEMA23#Assembly.Base_MotorType) + 4), <<D>> + str(hiddenref(NEMA23#Assembly.Base_MotorType) + 4))
FEATURE [Spreadsheet::Sheet] Spreadsheet010  label="Стол"
  PythonMode = false
  ShowCells = 0
  TreeRank = 7
  cells = A1=Стіл; A2=Ширина столу; B2(StolShirina)=300; A3=Довжина стола; B3(StolDovjuna)=200; A4=Висота столу; B4(StolVusota)=29; A6=Поглиблення під боковий захист; B6(StolPazZahust)=9; A7=Ширина поглиблення під захист; B7(StolPazShuruna)=232; A9=Площадка під каретки; A10=Довжина; B10(StolKaretkaDovjuna)=180; A11=Ширина; B11(StolKaretkuShurina)=222; A12=Ширина каретки; B12(KaretkaShirina)=36; A13=Глибина паза під каретку; B13(KaretkaPaz)=3; A15=Паз під опору; A16=Ширина; B16(OporaShiruna)=72; A17=Довжина; B17(OporaDovjuna)=29; A18=Глибина пазу під опору; B18(OporaPaz)=3
